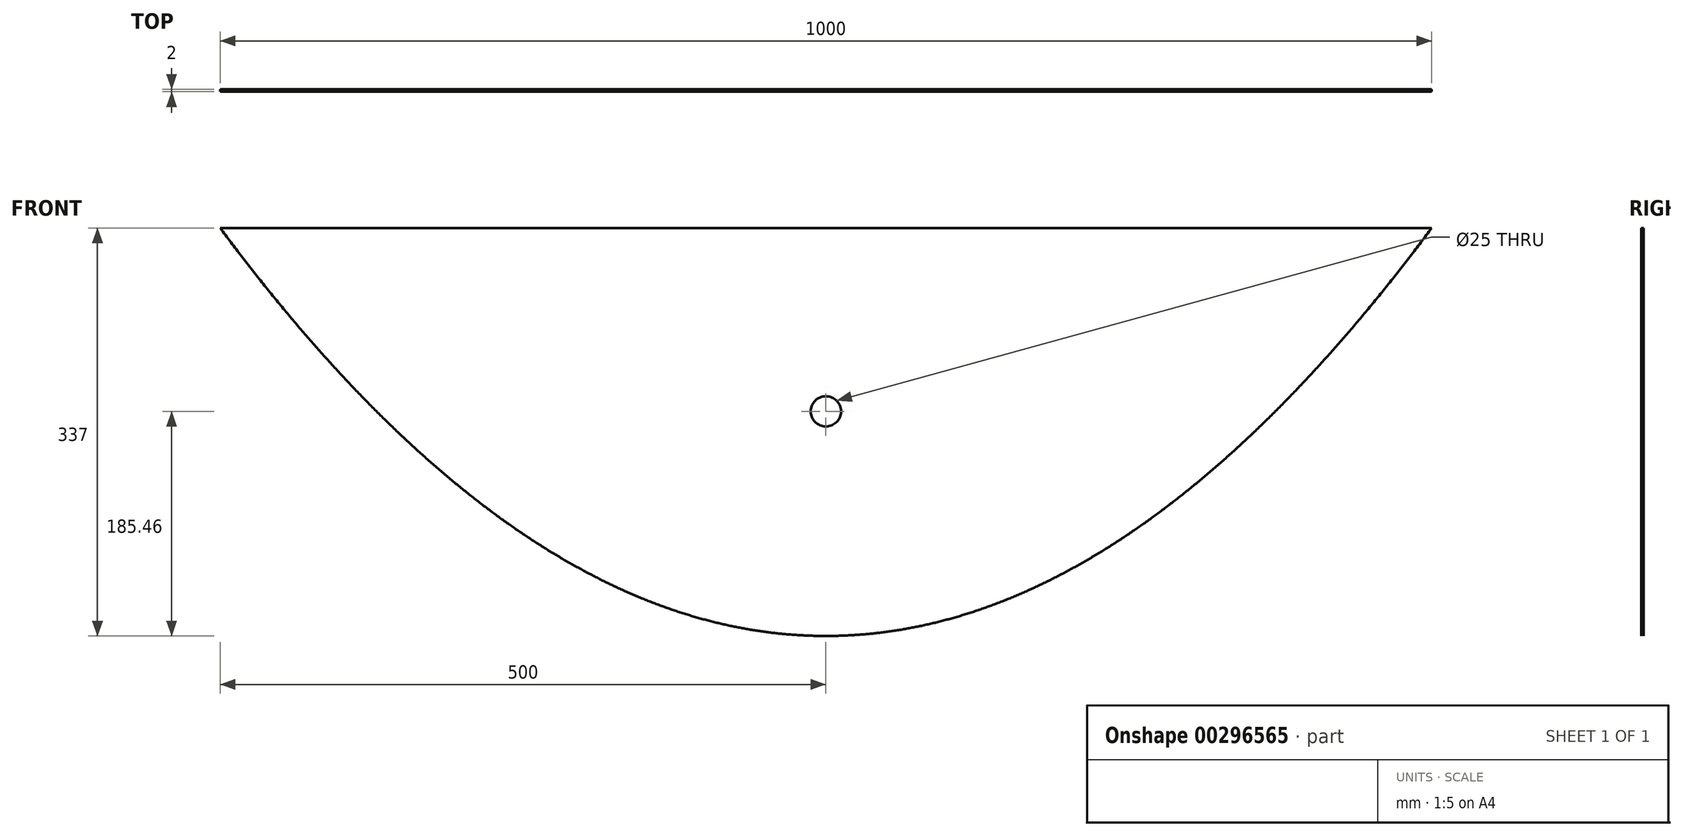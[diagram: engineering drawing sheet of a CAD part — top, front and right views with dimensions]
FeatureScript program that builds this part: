
annotation { "Feature Type Name" : "Feature", "Feature Type Description" : "" }
export const myFeature = defineFeature(function(context is Context, id is Id, definition is map)
    precondition{}
    {
        {
            var Q0;
            Q0=qCreatedBy(makeId("Front.planeOp"),FACE);
            var sketch = newSketch(context, id + "F0", { "sketchPlane" : qUnion([Q0])});
            skLineSegment(sketch, "E0", {"start": v(-500, 168.5) * mm, "end": v(-498.89, 167) * mm});
            skLineSegment(sketch, "E1", {"start": v(-498.89, 167) * mm, "end": v(-497.78, 165.5) * mm});
            skLineSegment(sketch, "E2", {"start": v(-497.78, 165.5) * mm, "end": v(-496.67, 164.02) * mm});
            skLineSegment(sketch, "E3", {"start": v(-496.67, 164.02) * mm, "end": v(-495.56, 162.53) * mm});
            skLineSegment(sketch, "E4", {"start": v(-495.56, 162.53) * mm, "end": v(-494.44, 161.05) * mm});
            skLineSegment(sketch, "E5", {"start": v(-494.44, 161.05) * mm, "end": v(-493.33, 159.57) * mm});
            skLineSegment(sketch, "E6", {"start": v(-493.33, 159.57) * mm, "end": v(-492.22, 158.1) * mm});
            skLineSegment(sketch, "E7", {"start": v(-492.22, 158.1) * mm, "end": v(-491.11, 156.62) * mm});
            skLineSegment(sketch, "E8", {"start": v(-491.11, 156.62) * mm, "end": v(-490, 155.15) * mm});
            skLineSegment(sketch, "E9", {"start": v(-490, 155.15) * mm, "end": v(-488.89, 153.69) * mm});
            skLineSegment(sketch, "E10", {"start": v(-488.89, 153.69) * mm, "end": v(-487.78, 152.22) * mm});
            skLineSegment(sketch, "E11", {"start": v(-487.78, 152.22) * mm, "end": v(-486.67, 150.76) * mm});
            skLineSegment(sketch, "E12", {"start": v(-486.67, 150.76) * mm, "end": v(-485.56, 149.3) * mm});
            skLineSegment(sketch, "E13", {"start": v(-485.56, 149.3) * mm, "end": v(-484.44, 147.86) * mm});
            skLineSegment(sketch, "E14", {"start": v(-484.44, 147.86) * mm, "end": v(-483.33, 146.4) * mm});
            skLineSegment(sketch, "E15", {"start": v(-483.33, 146.4) * mm, "end": v(-482.22, 144.96) * mm});
            skLineSegment(sketch, "E16", {"start": v(-482.22, 144.96) * mm, "end": v(-481.11, 143.52) * mm});
            skLineSegment(sketch, "E17", {"start": v(-481.11, 143.52) * mm, "end": v(-480, 142.08) * mm});
            skLineSegment(sketch, "E18", {"start": v(-480, 142.08) * mm, "end": v(-478.89, 140.64) * mm});
            skLineSegment(sketch, "E19", {"start": v(-478.89, 140.64) * mm, "end": v(-477.78, 139.2) * mm});
            skLineSegment(sketch, "E20", {"start": v(-477.78, 139.2) * mm, "end": v(-476.67, 137.78) * mm});
            skLineSegment(sketch, "E21", {"start": v(-476.67, 137.78) * mm, "end": v(-475.56, 136.35) * mm});
            skLineSegment(sketch, "E22", {"start": v(-475.56, 136.35) * mm, "end": v(-474.44, 134.93) * mm});
            skLineSegment(sketch, "E23", {"start": v(-474.44, 134.93) * mm, "end": v(-473.33, 133.5) * mm});
            skLineSegment(sketch, "E24", {"start": v(-473.33, 133.5) * mm, "end": v(-472.22, 132.1) * mm});
            skLineSegment(sketch, "E25", {"start": v(-472.22, 132.1) * mm, "end": v(-471.11, 130.68) * mm});
            skLineSegment(sketch, "E26", {"start": v(-471.11, 130.68) * mm, "end": v(-470, 129.27) * mm});
            skLineSegment(sketch, "E27", {"start": v(-470, 129.27) * mm, "end": v(-468.89, 127.86) * mm});
            skLineSegment(sketch, "E28", {"start": v(-468.89, 127.86) * mm, "end": v(-467.78, 126.46) * mm});
            skLineSegment(sketch, "E29", {"start": v(-467.78, 126.46) * mm, "end": v(-466.67, 125.06) * mm});
            skLineSegment(sketch, "E30", {"start": v(-466.67, 125.06) * mm, "end": v(-465.56, 123.67) * mm});
            skLineSegment(sketch, "E31", {"start": v(-465.56, 123.67) * mm, "end": v(-464.44, 122.27) * mm});
            skLineSegment(sketch, "E32", {"start": v(-464.44, 122.27) * mm, "end": v(-463.33, 120.88) * mm});
            skLineSegment(sketch, "E33", {"start": v(-463.33, 120.88) * mm, "end": v(-462.22, 119.5) * mm});
            skLineSegment(sketch, "E34", {"start": v(-462.22, 119.5) * mm, "end": v(-461.11, 118.11) * mm});
            skLineSegment(sketch, "E35", {"start": v(-461.11, 118.11) * mm, "end": v(-460, 116.73) * mm});
            skLineSegment(sketch, "E36", {"start": v(-460, 116.73) * mm, "end": v(-458.89, 115.36) * mm});
            skLineSegment(sketch, "E37", {"start": v(-458.89, 115.36) * mm, "end": v(-457.78, 113.99) * mm});
            skLineSegment(sketch, "E38", {"start": v(-457.78, 113.99) * mm, "end": v(-456.67, 112.62) * mm});
            skLineSegment(sketch, "E39", {"start": v(-456.67, 112.62) * mm, "end": v(-455.56, 111.25) * mm});
            skLineSegment(sketch, "E40", {"start": v(-455.56, 111.25) * mm, "end": v(-454.44, 109.89) * mm});
            skLineSegment(sketch, "E41", {"start": v(-454.44, 109.89) * mm, "end": v(-453.33, 108.53) * mm});
            skLineSegment(sketch, "E42", {"start": v(-453.33, 108.53) * mm, "end": v(-452.22, 107.17) * mm});
            skLineSegment(sketch, "E43", {"start": v(-452.22, 107.17) * mm, "end": v(-451.11, 105.82) * mm});
            skLineSegment(sketch, "E44", {"start": v(-451.11, 105.82) * mm, "end": v(-450, 104.47) * mm});
            skLineSegment(sketch, "E45", {"start": v(-450, 104.47) * mm, "end": v(-448.89, 103.12) * mm});
            skLineSegment(sketch, "E46", {"start": v(-448.89, 103.12) * mm, "end": v(-447.78, 101.78) * mm});
            skLineSegment(sketch, "E47", {"start": v(-447.78, 101.78) * mm, "end": v(-446.67, 100.44) * mm});
            skLineSegment(sketch, "E48", {"start": v(-446.67, 100.44) * mm, "end": v(-445.56, 99.1) * mm});
            skLineSegment(sketch, "E49", {"start": v(-445.56, 99.1) * mm, "end": v(-444.44, 97.77) * mm});
            skLineSegment(sketch, "E50", {"start": v(-444.44, 97.77) * mm, "end": v(-443.33, 96.44) * mm});
            skLineSegment(sketch, "E51", {"start": v(-443.33, 96.44) * mm, "end": v(-442.22, 95.11) * mm});
            skLineSegment(sketch, "E52", {"start": v(-442.22, 95.11) * mm, "end": v(-441.11, 93.8) * mm});
            skLineSegment(sketch, "E53", {"start": v(-441.11, 93.8) * mm, "end": v(-440, 92.47) * mm});
            skLineSegment(sketch, "E54", {"start": v(-440, 92.47) * mm, "end": v(-438.89, 91.15) * mm});
            skLineSegment(sketch, "E55", {"start": v(-438.89, 91.15) * mm, "end": v(-437.78, 89.84) * mm});
            skLineSegment(sketch, "E56", {"start": v(-437.78, 89.84) * mm, "end": v(-436.67, 88.53) * mm});
            skLineSegment(sketch, "E57", {"start": v(-436.67, 88.53) * mm, "end": v(-435.56, 87.23) * mm});
            skLineSegment(sketch, "E58", {"start": v(-435.56, 87.23) * mm, "end": v(-434.44, 85.92) * mm});
            skLineSegment(sketch, "E59", {"start": v(-434.44, 85.92) * mm, "end": v(-433.33, 84.62) * mm});
            skLineSegment(sketch, "E60", {"start": v(-433.33, 84.62) * mm, "end": v(-432.22, 83.33) * mm});
            skLineSegment(sketch, "E61", {"start": v(-432.22, 83.33) * mm, "end": v(-431.11, 82.03) * mm});
            skLineSegment(sketch, "E62", {"start": v(-431.11, 82.03) * mm, "end": v(-430, 80.74) * mm});
            skLineSegment(sketch, "E63", {"start": v(-430, 80.74) * mm, "end": v(-428.89, 79.46) * mm});
            skLineSegment(sketch, "E64", {"start": v(-428.89, 79.46) * mm, "end": v(-427.78, 78.17) * mm});
            skLineSegment(sketch, "E65", {"start": v(-427.78, 78.17) * mm, "end": v(-426.67, 76.9) * mm});
            skLineSegment(sketch, "E66", {"start": v(-426.67, 76.9) * mm, "end": v(-425.56, 75.62) * mm});
            skLineSegment(sketch, "E67", {"start": v(-425.56, 75.62) * mm, "end": v(-424.44, 74.34) * mm});
            skLineSegment(sketch, "E68", {"start": v(-424.44, 74.34) * mm, "end": v(-423.33, 73.07) * mm});
            skLineSegment(sketch, "E69", {"start": v(-423.33, 73.07) * mm, "end": v(-422.22, 71.8) * mm});
            skLineSegment(sketch, "E70", {"start": v(-422.22, 71.8) * mm, "end": v(-421.11, 70.54) * mm});
            skLineSegment(sketch, "E71", {"start": v(-421.11, 70.54) * mm, "end": v(-420, 69.29) * mm});
            skLineSegment(sketch, "E72", {"start": v(-420, 69.29) * mm, "end": v(-418.89, 68.03) * mm});
            skLineSegment(sketch, "E73", {"start": v(-418.89, 68.03) * mm, "end": v(-417.78, 66.78) * mm});
            skLineSegment(sketch, "E74", {"start": v(-417.78, 66.78) * mm, "end": v(-416.67, 65.53) * mm});
            skLineSegment(sketch, "E75", {"start": v(-416.67, 65.53) * mm, "end": v(-415.56, 64.28) * mm});
            skLineSegment(sketch, "E76", {"start": v(-415.56, 64.28) * mm, "end": v(-414.44, 63.04) * mm});
            skLineSegment(sketch, "E77", {"start": v(-414.44, 63.04) * mm, "end": v(-413.33, 61.8) * mm});
            skLineSegment(sketch, "E78", {"start": v(-413.33, 61.8) * mm, "end": v(-412.22, 60.56) * mm});
            skLineSegment(sketch, "E79", {"start": v(-412.22, 60.56) * mm, "end": v(-411.11, 59.33) * mm});
            skLineSegment(sketch, "E80", {"start": v(-411.11, 59.33) * mm, "end": v(-410, 58.1) * mm});
            skLineSegment(sketch, "E81", {"start": v(-410, 58.1) * mm, "end": v(-408.89, 56.87) * mm});
            skLineSegment(sketch, "E82", {"start": v(-408.89, 56.87) * mm, "end": v(-407.78, 55.65) * mm});
            skLineSegment(sketch, "E83", {"start": v(-407.78, 55.65) * mm, "end": v(-406.67, 54.43) * mm});
            skLineSegment(sketch, "E84", {"start": v(-406.67, 54.43) * mm, "end": v(-405.56, 53.21) * mm});
            skLineSegment(sketch, "E85", {"start": v(-405.56, 53.21) * mm, "end": v(-404.44, 52) * mm});
            skLineSegment(sketch, "E86", {"start": v(-404.44, 52) * mm, "end": v(-403.33, 50.79) * mm});
            skLineSegment(sketch, "E87", {"start": v(-403.33, 50.79) * mm, "end": v(-402.22, 49.58) * mm});
            skLineSegment(sketch, "E88", {"start": v(-402.22, 49.58) * mm, "end": v(-401.11, 48.38) * mm});
            skLineSegment(sketch, "E89", {"start": v(-401.11, 48.38) * mm, "end": v(-400, 47.18) * mm});
            skLineSegment(sketch, "E90", {"start": v(-400, 47.18) * mm, "end": v(-398.89, 45.98) * mm});
            skLineSegment(sketch, "E91", {"start": v(-398.89, 45.98) * mm, "end": v(-397.78, 44.79) * mm});
            skLineSegment(sketch, "E92", {"start": v(-397.78, 44.79) * mm, "end": v(-396.67, 43.6) * mm});
            skLineSegment(sketch, "E93", {"start": v(-396.67, 43.6) * mm, "end": v(-395.56, 42.41) * mm});
            skLineSegment(sketch, "E94", {"start": v(-395.56, 42.41) * mm, "end": v(-394.44, 41.23) * mm});
            skLineSegment(sketch, "E95", {"start": v(-394.44, 41.23) * mm, "end": v(-393.33, 40.05) * mm});
            skLineSegment(sketch, "E96", {"start": v(-393.33, 40.05) * mm, "end": v(-392.22, 38.87) * mm});
            skLineSegment(sketch, "E97", {"start": v(-392.22, 38.87) * mm, "end": v(-391.11, 37.7) * mm});
            skLineSegment(sketch, "E98", {"start": v(-391.11, 37.7) * mm, "end": v(-390, 36.53) * mm});
            skLineSegment(sketch, "E99", {"start": v(-390, 36.53) * mm, "end": v(-388.89, 35.36) * mm});
            skLineSegment(sketch, "E100", {"start": v(-388.89, 35.36) * mm, "end": v(-387.78, 34.2) * mm});
            skLineSegment(sketch, "E101", {"start": v(-387.78, 34.2) * mm, "end": v(-386.67, 33.04) * mm});
            skLineSegment(sketch, "E102", {"start": v(-386.67, 33.04) * mm, "end": v(-385.56, 31.88) * mm});
            skLineSegment(sketch, "E103", {"start": v(-385.56, 31.88) * mm, "end": v(-384.44, 30.73) * mm});
            skLineSegment(sketch, "E104", {"start": v(-384.44, 30.73) * mm, "end": v(-383.33, 29.58) * mm});
            skLineSegment(sketch, "E105", {"start": v(-383.33, 29.58) * mm, "end": v(-382.22, 28.43) * mm});
            skLineSegment(sketch, "E106", {"start": v(-382.22, 28.43) * mm, "end": v(-381.11, 27.29) * mm});
            skLineSegment(sketch, "E107", {"start": v(-381.11, 27.29) * mm, "end": v(-380, 26.15) * mm});
            skLineSegment(sketch, "E108", {"start": v(-380, 26.15) * mm, "end": v(-378.89, 25.01) * mm});
            skLineSegment(sketch, "E109", {"start": v(-378.89, 25.01) * mm, "end": v(-377.78, 23.88) * mm});
            skLineSegment(sketch, "E110", {"start": v(-377.78, 23.88) * mm, "end": v(-376.67, 22.75) * mm});
            skLineSegment(sketch, "E111", {"start": v(-376.67, 22.75) * mm, "end": v(-375.56, 21.62) * mm});
            skLineSegment(sketch, "E112", {"start": v(-375.56, 21.62) * mm, "end": v(-374.44, 20.5) * mm});
            skLineSegment(sketch, "E113", {"start": v(-374.44, 20.5) * mm, "end": v(-373.33, 19.38) * mm});
            skLineSegment(sketch, "E114", {"start": v(-373.33, 19.38) * mm, "end": v(-372.22, 18.26) * mm});
            skLineSegment(sketch, "E115", {"start": v(-372.22, 18.26) * mm, "end": v(-371.11, 17.15) * mm});
            skLineSegment(sketch, "E116", {"start": v(-371.11, 17.15) * mm, "end": v(-370, 16.04) * mm});
            skLineSegment(sketch, "E117", {"start": v(-370, 16.04) * mm, "end": v(-368.89, 14.93) * mm});
            skLineSegment(sketch, "E118", {"start": v(-368.89, 14.93) * mm, "end": v(-367.78, 13.83) * mm});
            skLineSegment(sketch, "E119", {"start": v(-367.78, 13.83) * mm, "end": v(-366.67, 12.73) * mm});
            skLineSegment(sketch, "E120", {"start": v(-366.67, 12.73) * mm, "end": v(-365.56, 11.63) * mm});
            skLineSegment(sketch, "E121", {"start": v(-365.56, 11.63) * mm, "end": v(-364.44, 10.54) * mm});
            skLineSegment(sketch, "E122", {"start": v(-364.44, 10.54) * mm, "end": v(-363.33, 9.45) * mm});
            skLineSegment(sketch, "E123", {"start": v(-363.33, 9.45) * mm, "end": v(-362.22, 8.36) * mm});
            skLineSegment(sketch, "E124", {"start": v(-362.22, 8.36) * mm, "end": v(-361.11, 7.28) * mm});
            skLineSegment(sketch, "E125", {"start": v(-361.11, 7.28) * mm, "end": v(-360, 6.2) * mm});
            skLineSegment(sketch, "E126", {"start": v(-360, 6.2) * mm, "end": v(-358.89, 5.12) * mm});
            skLineSegment(sketch, "E127", {"start": v(-358.89, 5.12) * mm, "end": v(-357.78, 4.05) * mm});
            skLineSegment(sketch, "E128", {"start": v(-357.78, 4.05) * mm, "end": v(-356.67, 2.98) * mm});
            skLineSegment(sketch, "E129", {"start": v(-356.67, 2.98) * mm, "end": v(-355.56, 1.91) * mm});
            skLineSegment(sketch, "E130", {"start": v(-355.56, 1.91) * mm, "end": v(-354.44, 0.85) * mm});
            skLineSegment(sketch, "E131", {"start": v(-354.44, 0.85) * mm, "end": v(-353.33, -0.21) * mm});
            skLineSegment(sketch, "E132", {"start": v(-353.33, -0.21) * mm, "end": v(-352.22, -1.27) * mm});
            skLineSegment(sketch, "E133", {"start": v(-352.22, -1.27) * mm, "end": v(-351.11, -2.32) * mm});
            skLineSegment(sketch, "E134", {"start": v(-351.11, -2.32) * mm, "end": v(-350, -3.37) * mm});
            skLineSegment(sketch, "E135", {"start": v(-350, -3.37) * mm, "end": v(-348.89, -4.42) * mm});
            skLineSegment(sketch, "E136", {"start": v(-348.89, -4.42) * mm, "end": v(-347.78, -5.46) * mm});
            skLineSegment(sketch, "E137", {"start": v(-347.78, -5.46) * mm, "end": v(-346.67, -6.5) * mm});
            skLineSegment(sketch, "E138", {"start": v(-346.67, -6.5) * mm, "end": v(-345.56, -7.54) * mm});
            skLineSegment(sketch, "E139", {"start": v(-345.56, -7.54) * mm, "end": v(-344.44, -8.57) * mm});
            skLineSegment(sketch, "E140", {"start": v(-344.44, -8.57) * mm, "end": v(-343.33, -9.6) * mm});
            skLineSegment(sketch, "E141", {"start": v(-343.33, -9.6) * mm, "end": v(-342.22, -10.63) * mm});
            skLineSegment(sketch, "E142", {"start": v(-342.22, -10.63) * mm, "end": v(-341.11, -11.65) * mm});
            skLineSegment(sketch, "E143", {"start": v(-341.11, -11.65) * mm, "end": v(-340, -12.67) * mm});
            skLineSegment(sketch, "E144", {"start": v(-340, -12.67) * mm, "end": v(-338.89, -13.7) * mm});
            skLineSegment(sketch, "E145", {"start": v(-338.89, -13.7) * mm, "end": v(-337.78, -14.7) * mm});
            skLineSegment(sketch, "E146", {"start": v(-337.78, -14.7) * mm, "end": v(-336.67, -15.71) * mm});
            skLineSegment(sketch, "E147", {"start": v(-336.67, -15.71) * mm, "end": v(-335.56, -16.72) * mm});
            skLineSegment(sketch, "E148", {"start": v(-335.56, -16.72) * mm, "end": v(-334.44, -17.72) * mm});
            skLineSegment(sketch, "E149", {"start": v(-334.44, -17.72) * mm, "end": v(-333.33, -18.72) * mm});
            skLineSegment(sketch, "E150", {"start": v(-333.33, -18.72) * mm, "end": v(-332.22, -19.72) * mm});
            skLineSegment(sketch, "E151", {"start": v(-332.22, -19.72) * mm, "end": v(-331.11, -20.71) * mm});
            skLineSegment(sketch, "E152", {"start": v(-331.11, -20.71) * mm, "end": v(-330, -21.7) * mm});
            skLineSegment(sketch, "E153", {"start": v(-330, -21.7) * mm, "end": v(-328.89, -22.7) * mm});
            skLineSegment(sketch, "E154", {"start": v(-328.89, -22.7) * mm, "end": v(-327.78, -23.68) * mm});
            skLineSegment(sketch, "E155", {"start": v(-327.78, -23.68) * mm, "end": v(-326.67, -24.66) * mm});
            skLineSegment(sketch, "E156", {"start": v(-326.67, -24.66) * mm, "end": v(-325.56, -25.63) * mm});
            skLineSegment(sketch, "E157", {"start": v(-325.56, -25.63) * mm, "end": v(-324.44, -26.6) * mm});
            skLineSegment(sketch, "E158", {"start": v(-324.44, -26.6) * mm, "end": v(-323.33, -27.58) * mm});
            skLineSegment(sketch, "E159", {"start": v(-323.33, -27.58) * mm, "end": v(-322.22, -28.54) * mm});
            skLineSegment(sketch, "E160", {"start": v(-322.22, -28.54) * mm, "end": v(-321.11, -29.5) * mm});
            skLineSegment(sketch, "E161", {"start": v(-321.11, -29.5) * mm, "end": v(-320, -30.47) * mm});
            skLineSegment(sketch, "E162", {"start": v(-320, -30.47) * mm, "end": v(-318.89, -31.42) * mm});
            skLineSegment(sketch, "E163", {"start": v(-318.89, -31.42) * mm, "end": v(-317.78, -32.38) * mm});
            skLineSegment(sketch, "E164", {"start": v(-317.78, -32.38) * mm, "end": v(-316.67, -33.33) * mm});
            skLineSegment(sketch, "E165", {"start": v(-316.67, -33.33) * mm, "end": v(-315.56, -34.27) * mm});
            skLineSegment(sketch, "E166", {"start": v(-315.56, -34.27) * mm, "end": v(-314.44, -35.22) * mm});
            skLineSegment(sketch, "E167", {"start": v(-314.44, -35.22) * mm, "end": v(-313.33, -36.16) * mm});
            skLineSegment(sketch, "E168", {"start": v(-313.33, -36.16) * mm, "end": v(-312.22, -37.1) * mm});
            skLineSegment(sketch, "E169", {"start": v(-312.22, -37.1) * mm, "end": v(-311.11, -38.03) * mm});
            skLineSegment(sketch, "E170", {"start": v(-311.11, -38.03) * mm, "end": v(-310, -38.96) * mm});
            skLineSegment(sketch, "E171", {"start": v(-310, -38.96) * mm, "end": v(-308.89, -39.89) * mm});
            skLineSegment(sketch, "E172", {"start": v(-308.89, -39.89) * mm, "end": v(-307.78, -40.8) * mm});
            skLineSegment(sketch, "E173", {"start": v(-307.78, -40.8) * mm, "end": v(-306.67, -41.73) * mm});
            skLineSegment(sketch, "E174", {"start": v(-306.67, -41.73) * mm, "end": v(-305.56, -42.65) * mm});
            skLineSegment(sketch, "E175", {"start": v(-305.56, -42.65) * mm, "end": v(-304.44, -43.56) * mm});
            skLineSegment(sketch, "E176", {"start": v(-304.44, -43.56) * mm, "end": v(-303.33, -44.47) * mm});
            skLineSegment(sketch, "E177", {"start": v(-303.33, -44.47) * mm, "end": v(-302.22, -45.38) * mm});
            skLineSegment(sketch, "E178", {"start": v(-302.22, -45.38) * mm, "end": v(-301.11, -46.28) * mm});
            skLineSegment(sketch, "E179", {"start": v(-301.11, -46.28) * mm, "end": v(-300, -47.18) * mm});
            skLineSegment(sketch, "E180", {"start": v(-300, -47.18) * mm, "end": v(-298.89, -48.08) * mm});
            skLineSegment(sketch, "E181", {"start": v(-298.89, -48.08) * mm, "end": v(-297.78, -48.97) * mm});
            skLineSegment(sketch, "E182", {"start": v(-297.78, -48.97) * mm, "end": v(-296.67, -49.86) * mm});
            skLineSegment(sketch, "E183", {"start": v(-296.67, -49.86) * mm, "end": v(-295.56, -50.75) * mm});
            skLineSegment(sketch, "E184", {"start": v(-295.56, -50.75) * mm, "end": v(-294.44, -51.63) * mm});
            skLineSegment(sketch, "E185", {"start": v(-294.44, -51.63) * mm, "end": v(-293.33, -52.51) * mm});
            skLineSegment(sketch, "E186", {"start": v(-293.33, -52.51) * mm, "end": v(-292.22, -53.4) * mm});
            skLineSegment(sketch, "E187", {"start": v(-292.22, -53.4) * mm, "end": v(-291.11, -54.26) * mm});
            skLineSegment(sketch, "E188", {"start": v(-291.11, -54.26) * mm, "end": v(-290, -55.14) * mm});
            skLineSegment(sketch, "E189", {"start": v(-290, -55.14) * mm, "end": v(-288.89, -56) * mm});
            skLineSegment(sketch, "E190", {"start": v(-288.89, -56) * mm, "end": v(-287.78, -56.87) * mm});
            skLineSegment(sketch, "E191", {"start": v(-287.78, -56.87) * mm, "end": v(-286.67, -57.73) * mm});
            skLineSegment(sketch, "E192", {"start": v(-286.67, -57.73) * mm, "end": v(-285.56, -58.58) * mm});
            skLineSegment(sketch, "E193", {"start": v(-285.56, -58.58) * mm, "end": v(-284.44, -59.44) * mm});
            skLineSegment(sketch, "E194", {"start": v(-284.44, -59.44) * mm, "end": v(-283.33, -60.29) * mm});
            skLineSegment(sketch, "E195", {"start": v(-283.33, -60.29) * mm, "end": v(-282.22, -61.13) * mm});
            skLineSegment(sketch, "E196", {"start": v(-282.22, -61.13) * mm, "end": v(-281.11, -61.98) * mm});
            skLineSegment(sketch, "E197", {"start": v(-281.11, -61.98) * mm, "end": v(-280, -62.82) * mm});
            skLineSegment(sketch, "E198", {"start": v(-280, -62.82) * mm, "end": v(-278.89, -63.66) * mm});
            skLineSegment(sketch, "E199", {"start": v(-278.89, -63.66) * mm, "end": v(-277.78, -64.49) * mm});
            skLineSegment(sketch, "E200", {"start": v(-277.78, -64.49) * mm, "end": v(-276.67, -65.32) * mm});
            skLineSegment(sketch, "E201", {"start": v(-276.67, -65.32) * mm, "end": v(-275.56, -66.15) * mm});
            skLineSegment(sketch, "E202", {"start": v(-275.56, -66.15) * mm, "end": v(-274.44, -66.97) * mm});
            skLineSegment(sketch, "E203", {"start": v(-274.44, -66.97) * mm, "end": v(-273.33, -67.8) * mm});
            skLineSegment(sketch, "E204", {"start": v(-273.33, -67.8) * mm, "end": v(-272.22, -68.6) * mm});
            skLineSegment(sketch, "E205", {"start": v(-272.22, -68.6) * mm, "end": v(-271.11, -69.42) * mm});
            skLineSegment(sketch, "E206", {"start": v(-271.11, -69.42) * mm, "end": v(-270, -70.23) * mm});
            skLineSegment(sketch, "E207", {"start": v(-270, -70.23) * mm, "end": v(-268.89, -71.04) * mm});
            skLineSegment(sketch, "E208", {"start": v(-268.89, -71.04) * mm, "end": v(-267.78, -71.84) * mm});
            skLineSegment(sketch, "E209", {"start": v(-267.78, -71.84) * mm, "end": v(-266.67, -72.64) * mm});
            skLineSegment(sketch, "E210", {"start": v(-266.67, -72.64) * mm, "end": v(-265.56, -73.44) * mm});
            skLineSegment(sketch, "E211", {"start": v(-265.56, -73.44) * mm, "end": v(-264.44, -74.24) * mm});
            skLineSegment(sketch, "E212", {"start": v(-264.44, -74.24) * mm, "end": v(-263.33, -75.03) * mm});
            skLineSegment(sketch, "E213", {"start": v(-263.33, -75.03) * mm, "end": v(-262.22, -75.81) * mm});
            skLineSegment(sketch, "E214", {"start": v(-262.22, -75.81) * mm, "end": v(-261.11, -76.6) * mm});
            skLineSegment(sketch, "E215", {"start": v(-261.11, -76.6) * mm, "end": v(-260, -77.38) * mm});
            skLineSegment(sketch, "E216", {"start": v(-260, -77.38) * mm, "end": v(-258.89, -78.15) * mm});
            skLineSegment(sketch, "E217", {"start": v(-258.89, -78.15) * mm, "end": v(-257.78, -78.93) * mm});
            skLineSegment(sketch, "E218", {"start": v(-257.78, -78.93) * mm, "end": v(-256.67, -79.7) * mm});
            skLineSegment(sketch, "E219", {"start": v(-256.67, -79.7) * mm, "end": v(-255.56, -80.47) * mm});
            skLineSegment(sketch, "E220", {"start": v(-255.56, -80.47) * mm, "end": v(-254.44, -81.23) * mm});
            skLineSegment(sketch, "E221", {"start": v(-254.44, -81.23) * mm, "end": v(-253.33, -82) * mm});
            skLineSegment(sketch, "E222", {"start": v(-253.33, -82) * mm, "end": v(-252.22, -82.75) * mm});
            skLineSegment(sketch, "E223", {"start": v(-252.22, -82.75) * mm, "end": v(-251.11, -83.5) * mm});
            skLineSegment(sketch, "E224", {"start": v(-251.11, -83.5) * mm, "end": v(-250, -84.25) * mm});
            skLineSegment(sketch, "E225", {"start": v(-250, -84.25) * mm, "end": v(-248.89, -85) * mm});
            skLineSegment(sketch, "E226", {"start": v(-248.89, -85) * mm, "end": v(-247.78, -85.74) * mm});
            skLineSegment(sketch, "E227", {"start": v(-247.78, -85.74) * mm, "end": v(-246.67, -86.48) * mm});
            skLineSegment(sketch, "E228", {"start": v(-246.67, -86.48) * mm, "end": v(-245.56, -87.22) * mm});
            skLineSegment(sketch, "E229", {"start": v(-245.56, -87.22) * mm, "end": v(-244.44, -87.95) * mm});
            skLineSegment(sketch, "E230", {"start": v(-244.44, -87.95) * mm, "end": v(-243.33, -88.69) * mm});
            skLineSegment(sketch, "E231", {"start": v(-243.33, -88.69) * mm, "end": v(-242.22, -89.41) * mm});
            skLineSegment(sketch, "E232", {"start": v(-242.22, -89.41) * mm, "end": v(-241.11, -90.14) * mm});
            skLineSegment(sketch, "E233", {"start": v(-241.11, -90.14) * mm, "end": v(-240, -90.86) * mm});
            skLineSegment(sketch, "E234", {"start": v(-240, -90.86) * mm, "end": v(-238.89, -91.57) * mm});
            skLineSegment(sketch, "E235", {"start": v(-238.89, -91.57) * mm, "end": v(-237.78, -92.29) * mm});
            skLineSegment(sketch, "E236", {"start": v(-237.78, -92.29) * mm, "end": v(-236.67, -93) * mm});
            skLineSegment(sketch, "E237", {"start": v(-236.67, -93) * mm, "end": v(-235.56, -93.7) * mm});
            skLineSegment(sketch, "E238", {"start": v(-235.56, -93.7) * mm, "end": v(-234.44, -94.41) * mm});
            skLineSegment(sketch, "E239", {"start": v(-234.44, -94.41) * mm, "end": v(-233.33, -95.11) * mm});
            skLineSegment(sketch, "E240", {"start": v(-233.33, -95.11) * mm, "end": v(-232.22, -95.8) * mm});
            skLineSegment(sketch, "E241", {"start": v(-232.22, -95.8) * mm, "end": v(-231.11, -96.5) * mm});
            skLineSegment(sketch, "E242", {"start": v(-231.11, -96.5) * mm, "end": v(-230, -97.2) * mm});
            skLineSegment(sketch, "E243", {"start": v(-230, -97.2) * mm, "end": v(-228.89, -97.88) * mm});
            skLineSegment(sketch, "E244", {"start": v(-228.89, -97.88) * mm, "end": v(-227.78, -98.56) * mm});
            skLineSegment(sketch, "E245", {"start": v(-227.78, -98.56) * mm, "end": v(-226.67, -99.24) * mm});
            skLineSegment(sketch, "E246", {"start": v(-226.67, -99.24) * mm, "end": v(-225.56, -99.92) * mm});
            skLineSegment(sketch, "E247", {"start": v(-225.56, -99.92) * mm, "end": v(-224.44, -100.6) * mm});
            skLineSegment(sketch, "E248", {"start": v(-224.44, -100.6) * mm, "end": v(-223.33, -101.27) * mm});
            skLineSegment(sketch, "E249", {"start": v(-223.33, -101.27) * mm, "end": v(-222.22, -101.93) * mm});
            skLineSegment(sketch, "E250", {"start": v(-222.22, -101.93) * mm, "end": v(-221.11, -102.6) * mm});
            skLineSegment(sketch, "E251", {"start": v(-221.11, -102.6) * mm, "end": v(-220, -103.26) * mm});
            skLineSegment(sketch, "E252", {"start": v(-220, -103.26) * mm, "end": v(-218.89, -103.92) * mm});
            skLineSegment(sketch, "E253", {"start": v(-218.89, -103.92) * mm, "end": v(-217.78, -104.57) * mm});
            skLineSegment(sketch, "E254", {"start": v(-217.78, -104.57) * mm, "end": v(-216.67, -105.22) * mm});
            skLineSegment(sketch, "E255", {"start": v(-216.67, -105.22) * mm, "end": v(-215.56, -105.87) * mm});
            skLineSegment(sketch, "E256", {"start": v(-215.56, -105.87) * mm, "end": v(-214.44, -106.51) * mm});
            skLineSegment(sketch, "E257", {"start": v(-214.44, -106.51) * mm, "end": v(-213.33, -107.15) * mm});
            skLineSegment(sketch, "E258", {"start": v(-213.33, -107.15) * mm, "end": v(-212.22, -107.8) * mm});
            skLineSegment(sketch, "E259", {"start": v(-212.22, -107.8) * mm, "end": v(-211.11, -108.42) * mm});
            skLineSegment(sketch, "E260", {"start": v(-211.11, -108.42) * mm, "end": v(-210, -109.06) * mm});
            skLineSegment(sketch, "E261", {"start": v(-210, -109.06) * mm, "end": v(-208.89, -109.68) * mm});
            skLineSegment(sketch, "E262", {"start": v(-208.89, -109.68) * mm, "end": v(-207.78, -110.3) * mm});
            skLineSegment(sketch, "E263", {"start": v(-207.78, -110.3) * mm, "end": v(-206.67, -110.93) * mm});
            skLineSegment(sketch, "E264", {"start": v(-206.67, -110.93) * mm, "end": v(-205.56, -111.54) * mm});
            skLineSegment(sketch, "E265", {"start": v(-205.56, -111.54) * mm, "end": v(-204.44, -112.16) * mm});
            skLineSegment(sketch, "E266", {"start": v(-204.44, -112.16) * mm, "end": v(-203.33, -112.77) * mm});
            skLineSegment(sketch, "E267", {"start": v(-203.33, -112.77) * mm, "end": v(-202.22, -113.38) * mm});
            skLineSegment(sketch, "E268", {"start": v(-202.22, -113.38) * mm, "end": v(-201.11, -113.98) * mm});
            skLineSegment(sketch, "E269", {"start": v(-201.11, -113.98) * mm, "end": v(-200, -114.58) * mm});
            skLineSegment(sketch, "E270", {"start": v(-200, -114.58) * mm, "end": v(-198.89, -115.18) * mm});
            skLineSegment(sketch, "E271", {"start": v(-198.89, -115.18) * mm, "end": v(-197.78, -115.77) * mm});
            skLineSegment(sketch, "E272", {"start": v(-197.78, -115.77) * mm, "end": v(-196.67, -116.36) * mm});
            skLineSegment(sketch, "E273", {"start": v(-196.67, -116.36) * mm, "end": v(-195.56, -116.95) * mm});
            skLineSegment(sketch, "E274", {"start": v(-195.56, -116.95) * mm, "end": v(-194.44, -117.54) * mm});
            skLineSegment(sketch, "E275", {"start": v(-194.44, -117.54) * mm, "end": v(-193.33, -118.12) * mm});
            skLineSegment(sketch, "E276", {"start": v(-193.33, -118.12) * mm, "end": v(-192.22, -118.7) * mm});
            skLineSegment(sketch, "E277", {"start": v(-192.22, -118.7) * mm, "end": v(-191.11, -119.27) * mm});
            skLineSegment(sketch, "E278", {"start": v(-191.11, -119.27) * mm, "end": v(-190, -119.84) * mm});
            skLineSegment(sketch, "E279", {"start": v(-190, -119.84) * mm, "end": v(-188.89, -120.4) * mm});
            skLineSegment(sketch, "E280", {"start": v(-188.89, -120.4) * mm, "end": v(-187.78, -120.97) * mm});
            skLineSegment(sketch, "E281", {"start": v(-187.78, -120.97) * mm, "end": v(-186.67, -121.53) * mm});
            skLineSegment(sketch, "E282", {"start": v(-186.67, -121.53) * mm, "end": v(-185.56, -122.09) * mm});
            skLineSegment(sketch, "E283", {"start": v(-185.56, -122.09) * mm, "end": v(-184.44, -122.64) * mm});
            skLineSegment(sketch, "E284", {"start": v(-184.44, -122.64) * mm, "end": v(-183.33, -123.2) * mm});
            skLineSegment(sketch, "E285", {"start": v(-183.33, -123.2) * mm, "end": v(-182.22, -123.74) * mm});
            skLineSegment(sketch, "E286", {"start": v(-182.22, -123.74) * mm, "end": v(-181.11, -124.29) * mm});
            skLineSegment(sketch, "E287", {"start": v(-181.11, -124.29) * mm, "end": v(-180, -124.83) * mm});
            skLineSegment(sketch, "E288", {"start": v(-180, -124.83) * mm, "end": v(-178.89, -125.36) * mm});
            skLineSegment(sketch, "E289", {"start": v(-178.89, -125.36) * mm, "end": v(-177.78, -125.9) * mm});
            skLineSegment(sketch, "E290", {"start": v(-177.78, -125.9) * mm, "end": v(-176.67, -126.43) * mm});
            skLineSegment(sketch, "E291", {"start": v(-176.67, -126.43) * mm, "end": v(-175.56, -126.96) * mm});
            skLineSegment(sketch, "E292", {"start": v(-175.56, -126.96) * mm, "end": v(-174.44, -127.48) * mm});
            skLineSegment(sketch, "E293", {"start": v(-174.44, -127.48) * mm, "end": v(-173.33, -128) * mm});
            skLineSegment(sketch, "E294", {"start": v(-173.33, -128) * mm, "end": v(-172.22, -128.52) * mm});
            skLineSegment(sketch, "E295", {"start": v(-172.22, -128.52) * mm, "end": v(-171.11, -129.03) * mm});
            skLineSegment(sketch, "E296", {"start": v(-171.11, -129.03) * mm, "end": v(-170, -129.54) * mm});
            skLineSegment(sketch, "E297", {"start": v(-170, -129.54) * mm, "end": v(-168.89, -130.05) * mm});
            skLineSegment(sketch, "E298", {"start": v(-168.89, -130.05) * mm, "end": v(-167.78, -130.56) * mm});
            skLineSegment(sketch, "E299", {"start": v(-167.78, -130.56) * mm, "end": v(-166.67, -131.06) * mm});
            skLineSegment(sketch, "E300", {"start": v(-166.67, -131.06) * mm, "end": v(-165.56, -131.56) * mm});
            skLineSegment(sketch, "E301", {"start": v(-165.56, -131.56) * mm, "end": v(-164.44, -132.05) * mm});
            skLineSegment(sketch, "E302", {"start": v(-164.44, -132.05) * mm, "end": v(-163.33, -132.54) * mm});
            skLineSegment(sketch, "E303", {"start": v(-163.33, -132.54) * mm, "end": v(-162.22, -133.03) * mm});
            skLineSegment(sketch, "E304", {"start": v(-162.22, -133.03) * mm, "end": v(-161.11, -133.51) * mm});
            skLineSegment(sketch, "E305", {"start": v(-161.11, -133.51) * mm, "end": v(-160, -134) * mm});
            skLineSegment(sketch, "E306", {"start": v(-160, -134) * mm, "end": v(-158.89, -134.47) * mm});
            skLineSegment(sketch, "E307", {"start": v(-158.89, -134.47) * mm, "end": v(-157.78, -134.94) * mm});
            skLineSegment(sketch, "E308", {"start": v(-157.78, -134.94) * mm, "end": v(-156.67, -135.42) * mm});
            skLineSegment(sketch, "E309", {"start": v(-156.67, -135.42) * mm, "end": v(-155.56, -135.88) * mm});
            skLineSegment(sketch, "E310", {"start": v(-155.56, -135.88) * mm, "end": v(-154.44, -136.35) * mm});
            skLineSegment(sketch, "E311", {"start": v(-154.44, -136.35) * mm, "end": v(-153.33, -136.8) * mm});
            skLineSegment(sketch, "E312", {"start": v(-153.33, -136.8) * mm, "end": v(-152.22, -137.27) * mm});
            skLineSegment(sketch, "E313", {"start": v(-152.22, -137.27) * mm, "end": v(-151.11, -137.72) * mm});
            skLineSegment(sketch, "E314", {"start": v(-151.11, -137.72) * mm, "end": v(-150, -138.17) * mm});
            skLineSegment(sketch, "E315", {"start": v(-150, -138.17) * mm, "end": v(-148.89, -138.62) * mm});
            skLineSegment(sketch, "E316", {"start": v(-148.89, -138.62) * mm, "end": v(-147.78, -139.06) * mm});
            skLineSegment(sketch, "E317", {"start": v(-147.78, -139.06) * mm, "end": v(-146.67, -139.5) * mm});
            skLineSegment(sketch, "E318", {"start": v(-146.67, -139.5) * mm, "end": v(-145.56, -139.94) * mm});
            skLineSegment(sketch, "E319", {"start": v(-145.56, -139.94) * mm, "end": v(-144.44, -140.38) * mm});
            skLineSegment(sketch, "E320", {"start": v(-144.44, -140.38) * mm, "end": v(-143.33, -140.8) * mm});
            skLineSegment(sketch, "E321", {"start": v(-143.33, -140.8) * mm, "end": v(-142.22, -141.24) * mm});
            skLineSegment(sketch, "E322", {"start": v(-142.22, -141.24) * mm, "end": v(-141.11, -141.66) * mm});
            skLineSegment(sketch, "E323", {"start": v(-141.11, -141.66) * mm, "end": v(-140, -142.08) * mm});
            skLineSegment(sketch, "E324", {"start": v(-140, -142.08) * mm, "end": v(-138.89, -142.5) * mm});
            skLineSegment(sketch, "E325", {"start": v(-138.89, -142.5) * mm, "end": v(-137.78, -142.91) * mm});
            skLineSegment(sketch, "E326", {"start": v(-137.78, -142.91) * mm, "end": v(-136.67, -143.32) * mm});
            skLineSegment(sketch, "E327", {"start": v(-136.67, -143.32) * mm, "end": v(-135.56, -143.73) * mm});
            skLineSegment(sketch, "E328", {"start": v(-135.56, -143.73) * mm, "end": v(-134.44, -144.14) * mm});
            skLineSegment(sketch, "E329", {"start": v(-134.44, -144.14) * mm, "end": v(-133.33, -144.54) * mm});
            skLineSegment(sketch, "E330", {"start": v(-133.33, -144.54) * mm, "end": v(-132.22, -144.94) * mm});
            skLineSegment(sketch, "E331", {"start": v(-132.22, -144.94) * mm, "end": v(-131.11, -145.33) * mm});
            skLineSegment(sketch, "E332", {"start": v(-131.11, -145.33) * mm, "end": v(-130, -145.72) * mm});
            skLineSegment(sketch, "E333", {"start": v(-130, -145.72) * mm, "end": v(-128.89, -146.1) * mm});
            skLineSegment(sketch, "E334", {"start": v(-128.89, -146.1) * mm, "end": v(-127.78, -146.5) * mm});
            skLineSegment(sketch, "E335", {"start": v(-127.78, -146.5) * mm, "end": v(-126.67, -146.87) * mm});
            skLineSegment(sketch, "E336", {"start": v(-126.67, -146.87) * mm, "end": v(-125.56, -147.25) * mm});
            skLineSegment(sketch, "E337", {"start": v(-125.56, -147.25) * mm, "end": v(-124.44, -147.63) * mm});
            skLineSegment(sketch, "E338", {"start": v(-124.44, -147.63) * mm, "end": v(-123.33, -148) * mm});
            skLineSegment(sketch, "E339", {"start": v(-123.33, -148) * mm, "end": v(-122.22, -148.36) * mm});
            skLineSegment(sketch, "E340", {"start": v(-122.22, -148.36) * mm, "end": v(-121.11, -148.73) * mm});
            skLineSegment(sketch, "E341", {"start": v(-121.11, -148.73) * mm, "end": v(-120, -149.1) * mm});
            skLineSegment(sketch, "E342", {"start": v(-120, -149.1) * mm, "end": v(-118.89, -149.45) * mm});
            skLineSegment(sketch, "E343", {"start": v(-118.89, -149.45) * mm, "end": v(-117.78, -149.8) * mm});
            skLineSegment(sketch, "E344", {"start": v(-117.78, -149.8) * mm, "end": v(-116.67, -150.15) * mm});
            skLineSegment(sketch, "E345", {"start": v(-116.67, -150.15) * mm, "end": v(-115.56, -150.5) * mm});
            skLineSegment(sketch, "E346", {"start": v(-115.56, -150.5) * mm, "end": v(-114.44, -150.85) * mm});
            skLineSegment(sketch, "E347", {"start": v(-114.44, -150.85) * mm, "end": v(-113.33, -151.19) * mm});
            skLineSegment(sketch, "E348", {"start": v(-113.33, -151.19) * mm, "end": v(-112.22, -151.53) * mm});
            skLineSegment(sketch, "E349", {"start": v(-112.22, -151.53) * mm, "end": v(-111.11, -151.86) * mm});
            skLineSegment(sketch, "E350", {"start": v(-111.11, -151.86) * mm, "end": v(-110, -152.2) * mm});
            skLineSegment(sketch, "E351", {"start": v(-110, -152.2) * mm, "end": v(-108.89, -152.52) * mm});
            skLineSegment(sketch, "E352", {"start": v(-108.89, -152.52) * mm, "end": v(-107.78, -152.84) * mm});
            skLineSegment(sketch, "E353", {"start": v(-107.78, -152.84) * mm, "end": v(-106.67, -153.16) * mm});
            skLineSegment(sketch, "E354", {"start": v(-106.67, -153.16) * mm, "end": v(-105.56, -153.48) * mm});
            skLineSegment(sketch, "E355", {"start": v(-105.56, -153.48) * mm, "end": v(-104.44, -153.8) * mm});
            skLineSegment(sketch, "E356", {"start": v(-104.44, -153.8) * mm, "end": v(-103.33, -154.1) * mm});
            skLineSegment(sketch, "E357", {"start": v(-103.33, -154.1) * mm, "end": v(-102.22, -154.42) * mm});
            skLineSegment(sketch, "E358", {"start": v(-102.22, -154.42) * mm, "end": v(-101.11, -154.72) * mm});
            skLineSegment(sketch, "E359", {"start": v(-101.11, -154.72) * mm, "end": v(-100, -155.02) * mm});
            skLineSegment(sketch, "E360", {"start": v(-100, -155.02) * mm, "end": v(-98.89, -155.32) * mm});
            skLineSegment(sketch, "E361", {"start": v(-98.89, -155.32) * mm, "end": v(-97.78, -155.61) * mm});
            skLineSegment(sketch, "E362", {"start": v(-97.78, -155.61) * mm, "end": v(-96.67, -155.9) * mm});
            skLineSegment(sketch, "E363", {"start": v(-96.67, -155.9) * mm, "end": v(-95.56, -156.2) * mm});
            skLineSegment(sketch, "E364", {"start": v(-95.56, -156.2) * mm, "end": v(-94.44, -156.48) * mm});
            skLineSegment(sketch, "E365", {"start": v(-94.44, -156.48) * mm, "end": v(-93.33, -156.76) * mm});
            skLineSegment(sketch, "E366", {"start": v(-93.33, -156.76) * mm, "end": v(-92.22, -157.04) * mm});
            skLineSegment(sketch, "E367", {"start": v(-92.22, -157.04) * mm, "end": v(-91.11, -157.31) * mm});
            skLineSegment(sketch, "E368", {"start": v(-91.11, -157.31) * mm, "end": v(-90, -157.58) * mm});
            skLineSegment(sketch, "E369", {"start": v(-90, -157.58) * mm, "end": v(-88.89, -157.85) * mm});
            skLineSegment(sketch, "E370", {"start": v(-88.89, -157.85) * mm, "end": v(-87.78, -158.12) * mm});
            skLineSegment(sketch, "E371", {"start": v(-87.78, -158.12) * mm, "end": v(-86.67, -158.38) * mm});
            skLineSegment(sketch, "E372", {"start": v(-86.67, -158.38) * mm, "end": v(-85.56, -158.63) * mm});
            skLineSegment(sketch, "E373", {"start": v(-85.56, -158.63) * mm, "end": v(-84.44, -158.89) * mm});
            skLineSegment(sketch, "E374", {"start": v(-84.44, -158.89) * mm, "end": v(-83.33, -159.14) * mm});
            skLineSegment(sketch, "E375", {"start": v(-83.33, -159.14) * mm, "end": v(-82.22, -159.39) * mm});
            skLineSegment(sketch, "E376", {"start": v(-82.22, -159.39) * mm, "end": v(-81.11, -159.63) * mm});
            skLineSegment(sketch, "E377", {"start": v(-81.11, -159.63) * mm, "end": v(-80, -159.87) * mm});
            skLineSegment(sketch, "E378", {"start": v(-80, -159.87) * mm, "end": v(-78.89, -160.11) * mm});
            skLineSegment(sketch, "E379", {"start": v(-78.89, -160.11) * mm, "end": v(-77.78, -160.35) * mm});
            skLineSegment(sketch, "E380", {"start": v(-77.78, -160.35) * mm, "end": v(-76.67, -160.58) * mm});
            skLineSegment(sketch, "E381", {"start": v(-76.67, -160.58) * mm, "end": v(-75.56, -160.8) * mm});
            skLineSegment(sketch, "E382", {"start": v(-75.56, -160.8) * mm, "end": v(-74.44, -161.03) * mm});
            skLineSegment(sketch, "E383", {"start": v(-74.44, -161.03) * mm, "end": v(-73.33, -161.25) * mm});
            skLineSegment(sketch, "E384", {"start": v(-73.33, -161.25) * mm, "end": v(-72.22, -161.47) * mm});
            skLineSegment(sketch, "E385", {"start": v(-72.22, -161.47) * mm, "end": v(-71.11, -161.69) * mm});
            skLineSegment(sketch, "E386", {"start": v(-71.11, -161.69) * mm, "end": v(-70, -161.9) * mm});
            skLineSegment(sketch, "E387", {"start": v(-70, -161.9) * mm, "end": v(-68.89, -162.1) * mm});
            skLineSegment(sketch, "E388", {"start": v(-68.89, -162.1) * mm, "end": v(-67.78, -162.3) * mm});
            skLineSegment(sketch, "E389", {"start": v(-67.78, -162.3) * mm, "end": v(-66.67, -162.51) * mm});
            skLineSegment(sketch, "E390", {"start": v(-66.67, -162.51) * mm, "end": v(-65.56, -162.7) * mm});
            skLineSegment(sketch, "E391", {"start": v(-65.56, -162.7) * mm, "end": v(-64.44, -162.9) * mm});
            skLineSegment(sketch, "E392", {"start": v(-64.44, -162.9) * mm, "end": v(-63.33, -163.1) * mm});
            skLineSegment(sketch, "E393", {"start": v(-63.33, -163.1) * mm, "end": v(-62.22, -163.28) * mm});
            skLineSegment(sketch, "E394", {"start": v(-62.22, -163.28) * mm, "end": v(-61.11, -163.47) * mm});
            skLineSegment(sketch, "E395", {"start": v(-61.11, -163.47) * mm, "end": v(-60, -163.65) * mm});
            skLineSegment(sketch, "E396", {"start": v(-60, -163.65) * mm, "end": v(-58.89, -163.83) * mm});
            skLineSegment(sketch, "E397", {"start": v(-58.89, -163.83) * mm, "end": v(-57.78, -164) * mm});
            skLineSegment(sketch, "E398", {"start": v(-57.78, -164) * mm, "end": v(-56.67, -164.17) * mm});
            skLineSegment(sketch, "E399", {"start": v(-56.67, -164.17) * mm, "end": v(-55.56, -164.34) * mm});
            skLineSegment(sketch, "E400", {"start": v(-55.56, -164.34) * mm, "end": v(-54.44, -164.5) * mm});
            skLineSegment(sketch, "E401", {"start": v(-54.44, -164.5) * mm, "end": v(-53.33, -164.67) * mm});
            skLineSegment(sketch, "E402", {"start": v(-53.33, -164.67) * mm, "end": v(-52.22, -164.83) * mm});
            skLineSegment(sketch, "E403", {"start": v(-52.22, -164.83) * mm, "end": v(-51.11, -164.98) * mm});
            skLineSegment(sketch, "E404", {"start": v(-51.11, -164.98) * mm, "end": v(-50, -165.13) * mm});
            skLineSegment(sketch, "E405", {"start": v(-50, -165.13) * mm, "end": v(-48.89, -165.28) * mm});
            skLineSegment(sketch, "E406", {"start": v(-48.89, -165.28) * mm, "end": v(-47.78, -165.42) * mm});
            skLineSegment(sketch, "E407", {"start": v(-47.78, -165.42) * mm, "end": v(-46.67, -165.57) * mm});
            skLineSegment(sketch, "E408", {"start": v(-46.67, -165.57) * mm, "end": v(-45.56, -165.7) * mm});
            skLineSegment(sketch, "E409", {"start": v(-45.56, -165.7) * mm, "end": v(-44.44, -165.84) * mm});
            skLineSegment(sketch, "E410", {"start": v(-44.44, -165.84) * mm, "end": v(-43.33, -165.97) * mm});
            skLineSegment(sketch, "E411", {"start": v(-43.33, -165.97) * mm, "end": v(-42.22, -166.1) * mm});
            skLineSegment(sketch, "E412", {"start": v(-42.22, -166.1) * mm, "end": v(-41.11, -166.22) * mm});
            skLineSegment(sketch, "E413", {"start": v(-41.11, -166.22) * mm, "end": v(-40, -166.34) * mm});
            skLineSegment(sketch, "E414", {"start": v(-40, -166.34) * mm, "end": v(-38.89, -166.46) * mm});
            skLineSegment(sketch, "E415", {"start": v(-38.89, -166.46) * mm, "end": v(-37.78, -166.58) * mm});
            skLineSegment(sketch, "E416", {"start": v(-37.78, -166.58) * mm, "end": v(-36.67, -166.69) * mm});
            skLineSegment(sketch, "E417", {"start": v(-36.67, -166.69) * mm, "end": v(-35.56, -166.8) * mm});
            skLineSegment(sketch, "E418", {"start": v(-35.56, -166.8) * mm, "end": v(-34.44, -166.9) * mm});
            skLineSegment(sketch, "E419", {"start": v(-34.44, -166.9) * mm, "end": v(-33.33, -167) * mm});
            skLineSegment(sketch, "E420", {"start": v(-33.33, -167) * mm, "end": v(-32.22, -167.1) * mm});
            skLineSegment(sketch, "E421", {"start": v(-32.22, -167.1) * mm, "end": v(-31.11, -167.2) * mm});
            skLineSegment(sketch, "E422", {"start": v(-31.11, -167.2) * mm, "end": v(-30, -167.29) * mm});
            skLineSegment(sketch, "E423", {"start": v(-30, -167.29) * mm, "end": v(-28.89, -167.38) * mm});
            skLineSegment(sketch, "E424", {"start": v(-28.89, -167.38) * mm, "end": v(-27.78, -167.46) * mm});
            skLineSegment(sketch, "E425", {"start": v(-27.78, -167.46) * mm, "end": v(-26.67, -167.54) * mm});
            skLineSegment(sketch, "E426", {"start": v(-26.67, -167.54) * mm, "end": v(-25.56, -167.62) * mm});
            skLineSegment(sketch, "E427", {"start": v(-25.56, -167.62) * mm, "end": v(-24.44, -167.7) * mm});
            skLineSegment(sketch, "E428", {"start": v(-24.44, -167.7) * mm, "end": v(-23.33, -167.77) * mm});
            skLineSegment(sketch, "E429", {"start": v(-23.33, -167.77) * mm, "end": v(-22.22, -167.84) * mm});
            skLineSegment(sketch, "E430", {"start": v(-22.22, -167.84) * mm, "end": v(-21.11, -167.9) * mm});
            skLineSegment(sketch, "E431", {"start": v(-21.11, -167.9) * mm, "end": v(-20, -167.96) * mm});
            skLineSegment(sketch, "E432", {"start": v(-20, -167.96) * mm, "end": v(-18.89, -168.02) * mm});
            skLineSegment(sketch, "E433", {"start": v(-18.89, -168.02) * mm, "end": v(-17.78, -168.08) * mm});
            skLineSegment(sketch, "E434", {"start": v(-17.78, -168.08) * mm, "end": v(-16.67, -168.13) * mm});
            skLineSegment(sketch, "E435", {"start": v(-16.67, -168.13) * mm, "end": v(-15.56, -168.18) * mm});
            skLineSegment(sketch, "E436", {"start": v(-15.56, -168.18) * mm, "end": v(-14.44, -168.22) * mm});
            skLineSegment(sketch, "E437", {"start": v(-14.44, -168.22) * mm, "end": v(-13.33, -168.26) * mm});
            skLineSegment(sketch, "E438", {"start": v(-13.33, -168.26) * mm, "end": v(-12.22, -168.3) * mm});
            skLineSegment(sketch, "E439", {"start": v(-12.22, -168.3) * mm, "end": v(-11.11, -168.33) * mm});
            skLineSegment(sketch, "E440", {"start": v(-11.11, -168.33) * mm, "end": v(-10, -168.37) * mm});
            skLineSegment(sketch, "E441", {"start": v(-10, -168.37) * mm, "end": v(-8.89, -168.4) * mm});
            skLineSegment(sketch, "E442", {"start": v(-8.89, -168.4) * mm, "end": v(-7.78, -168.42) * mm});
            skLineSegment(sketch, "E443", {"start": v(-7.78, -168.42) * mm, "end": v(-6.67, -168.44) * mm});
            skLineSegment(sketch, "E444", {"start": v(-6.67, -168.44) * mm, "end": v(-5.56, -168.46) * mm});
            skLineSegment(sketch, "E445", {"start": v(-5.56, -168.46) * mm, "end": v(-4.44, -168.47) * mm});
            skLineSegment(sketch, "E446", {"start": v(-4.44, -168.47) * mm, "end": v(-3.33, -168.49) * mm});
            skLineSegment(sketch, "E447", {"start": v(-3.33, -168.49) * mm, "end": v(-2.22, -168.5) * mm});
            skLineSegment(sketch, "E448", {"start": v(-2.22, -168.5) * mm, "end": v(-1.11, -168.5) * mm});
            skLineSegment(sketch, "E449", {"start": v(-1.11, -168.5) * mm, "end": v(0, -168.5) * mm});
            skLineSegment(sketch, "E450", {"start": v(0, -168.5) * mm, "end": v(1.11, -168.5) * mm});
            skLineSegment(sketch, "E451", {"start": v(1.11, -168.5) * mm, "end": v(2.22, -168.5) * mm});
            skLineSegment(sketch, "E452", {"start": v(2.22, -168.5) * mm, "end": v(3.33, -168.49) * mm});
            skLineSegment(sketch, "E453", {"start": v(3.33, -168.49) * mm, "end": v(4.44, -168.47) * mm});
            skLineSegment(sketch, "E454", {"start": v(4.44, -168.47) * mm, "end": v(5.56, -168.46) * mm});
            skLineSegment(sketch, "E455", {"start": v(5.56, -168.46) * mm, "end": v(6.67, -168.44) * mm});
            skLineSegment(sketch, "E456", {"start": v(6.67, -168.44) * mm, "end": v(7.78, -168.42) * mm});
            skLineSegment(sketch, "E457", {"start": v(7.78, -168.42) * mm, "end": v(8.89, -168.4) * mm});
            skLineSegment(sketch, "E458", {"start": v(8.89, -168.4) * mm, "end": v(10, -168.37) * mm});
            skLineSegment(sketch, "E459", {"start": v(10, -168.37) * mm, "end": v(11.11, -168.33) * mm});
            skLineSegment(sketch, "E460", {"start": v(11.11, -168.33) * mm, "end": v(12.22, -168.3) * mm});
            skLineSegment(sketch, "E461", {"start": v(12.22, -168.3) * mm, "end": v(13.33, -168.26) * mm});
            skLineSegment(sketch, "E462", {"start": v(13.33, -168.26) * mm, "end": v(14.44, -168.22) * mm});
            skLineSegment(sketch, "E463", {"start": v(14.44, -168.22) * mm, "end": v(15.56, -168.18) * mm});
            skLineSegment(sketch, "E464", {"start": v(15.56, -168.18) * mm, "end": v(16.67, -168.13) * mm});
            skLineSegment(sketch, "E465", {"start": v(16.67, -168.13) * mm, "end": v(17.78, -168.08) * mm});
            skLineSegment(sketch, "E466", {"start": v(17.78, -168.08) * mm, "end": v(18.89, -168.02) * mm});
            skLineSegment(sketch, "E467", {"start": v(18.89, -168.02) * mm, "end": v(20, -167.96) * mm});
            skLineSegment(sketch, "E468", {"start": v(20, -167.96) * mm, "end": v(21.11, -167.9) * mm});
            skLineSegment(sketch, "E469", {"start": v(21.11, -167.9) * mm, "end": v(22.22, -167.84) * mm});
            skLineSegment(sketch, "E470", {"start": v(22.22, -167.84) * mm, "end": v(23.33, -167.77) * mm});
            skLineSegment(sketch, "E471", {"start": v(23.33, -167.77) * mm, "end": v(24.44, -167.7) * mm});
            skLineSegment(sketch, "E472", {"start": v(24.44, -167.7) * mm, "end": v(25.56, -167.62) * mm});
            skLineSegment(sketch, "E473", {"start": v(25.56, -167.62) * mm, "end": v(26.67, -167.54) * mm});
            skLineSegment(sketch, "E474", {"start": v(26.67, -167.54) * mm, "end": v(27.78, -167.46) * mm});
            skLineSegment(sketch, "E475", {"start": v(27.78, -167.46) * mm, "end": v(28.89, -167.38) * mm});
            skLineSegment(sketch, "E476", {"start": v(28.89, -167.38) * mm, "end": v(30, -167.29) * mm});
            skLineSegment(sketch, "E477", {"start": v(30, -167.29) * mm, "end": v(31.11, -167.2) * mm});
            skLineSegment(sketch, "E478", {"start": v(31.11, -167.2) * mm, "end": v(32.22, -167.1) * mm});
            skLineSegment(sketch, "E479", {"start": v(32.22, -167.1) * mm, "end": v(33.33, -167) * mm});
            skLineSegment(sketch, "E480", {"start": v(33.33, -167) * mm, "end": v(34.44, -166.9) * mm});
            skLineSegment(sketch, "E481", {"start": v(34.44, -166.9) * mm, "end": v(35.56, -166.8) * mm});
            skLineSegment(sketch, "E482", {"start": v(35.56, -166.8) * mm, "end": v(36.67, -166.69) * mm});
            skLineSegment(sketch, "E483", {"start": v(36.67, -166.69) * mm, "end": v(37.78, -166.58) * mm});
            skLineSegment(sketch, "E484", {"start": v(37.78, -166.58) * mm, "end": v(38.89, -166.46) * mm});
            skLineSegment(sketch, "E485", {"start": v(38.89, -166.46) * mm, "end": v(40, -166.34) * mm});
            skLineSegment(sketch, "E486", {"start": v(40, -166.34) * mm, "end": v(41.11, -166.22) * mm});
            skLineSegment(sketch, "E487", {"start": v(41.11, -166.22) * mm, "end": v(42.22, -166.1) * mm});
            skLineSegment(sketch, "E488", {"start": v(42.22, -166.1) * mm, "end": v(43.33, -165.97) * mm});
            skLineSegment(sketch, "E489", {"start": v(43.33, -165.97) * mm, "end": v(44.44, -165.84) * mm});
            skLineSegment(sketch, "E490", {"start": v(44.44, -165.84) * mm, "end": v(45.56, -165.7) * mm});
            skLineSegment(sketch, "E491", {"start": v(45.56, -165.7) * mm, "end": v(46.67, -165.57) * mm});
            skLineSegment(sketch, "E492", {"start": v(46.67, -165.57) * mm, "end": v(47.78, -165.42) * mm});
            skLineSegment(sketch, "E493", {"start": v(47.78, -165.42) * mm, "end": v(48.89, -165.28) * mm});
            skLineSegment(sketch, "E494", {"start": v(48.89, -165.28) * mm, "end": v(50, -165.13) * mm});
            skLineSegment(sketch, "E495", {"start": v(50, -165.13) * mm, "end": v(51.11, -164.98) * mm});
            skLineSegment(sketch, "E496", {"start": v(51.11, -164.98) * mm, "end": v(52.22, -164.82) * mm});
            skLineSegment(sketch, "E497", {"start": v(52.22, -164.82) * mm, "end": v(53.33, -164.67) * mm});
            skLineSegment(sketch, "E498", {"start": v(53.33, -164.67) * mm, "end": v(54.44, -164.5) * mm});
            skLineSegment(sketch, "E499", {"start": v(54.44, -164.5) * mm, "end": v(55.56, -164.34) * mm});
            skLineSegment(sketch, "E500", {"start": v(55.56, -164.34) * mm, "end": v(56.67, -164.17) * mm});
            skLineSegment(sketch, "E501", {"start": v(56.67, -164.17) * mm, "end": v(57.78, -164) * mm});
            skLineSegment(sketch, "E502", {"start": v(57.78, -164) * mm, "end": v(58.89, -163.83) * mm});
            skLineSegment(sketch, "E503", {"start": v(58.89, -163.83) * mm, "end": v(60, -163.65) * mm});
            skLineSegment(sketch, "E504", {"start": v(60, -163.65) * mm, "end": v(61.11, -163.47) * mm});
            skLineSegment(sketch, "E505", {"start": v(61.11, -163.47) * mm, "end": v(62.22, -163.28) * mm});
            skLineSegment(sketch, "E506", {"start": v(62.22, -163.28) * mm, "end": v(63.33, -163.1) * mm});
            skLineSegment(sketch, "E507", {"start": v(63.33, -163.1) * mm, "end": v(64.44, -162.9) * mm});
            skLineSegment(sketch, "E508", {"start": v(64.44, -162.9) * mm, "end": v(65.56, -162.7) * mm});
            skLineSegment(sketch, "E509", {"start": v(65.56, -162.7) * mm, "end": v(66.67, -162.5) * mm});
            skLineSegment(sketch, "E510", {"start": v(66.67, -162.5) * mm, "end": v(67.78, -162.3) * mm});
            skLineSegment(sketch, "E511", {"start": v(67.78, -162.3) * mm, "end": v(68.89, -162.1) * mm});
            skLineSegment(sketch, "E512", {"start": v(68.89, -162.1) * mm, "end": v(70, -161.9) * mm});
            skLineSegment(sketch, "E513", {"start": v(70, -161.9) * mm, "end": v(71.11, -161.68) * mm});
            skLineSegment(sketch, "E514", {"start": v(71.11, -161.68) * mm, "end": v(72.22, -161.47) * mm});
            skLineSegment(sketch, "E515", {"start": v(72.22, -161.47) * mm, "end": v(73.33, -161.25) * mm});
            skLineSegment(sketch, "E516", {"start": v(73.33, -161.25) * mm, "end": v(74.44, -161.03) * mm});
            skLineSegment(sketch, "E517", {"start": v(74.44, -161.03) * mm, "end": v(75.56, -160.8) * mm});
            skLineSegment(sketch, "E518", {"start": v(75.56, -160.8) * mm, "end": v(76.67, -160.58) * mm});
            skLineSegment(sketch, "E519", {"start": v(76.67, -160.58) * mm, "end": v(77.78, -160.35) * mm});
            skLineSegment(sketch, "E520", {"start": v(77.78, -160.35) * mm, "end": v(78.89, -160.11) * mm});
            skLineSegment(sketch, "E521", {"start": v(78.89, -160.11) * mm, "end": v(80, -159.87) * mm});
            skLineSegment(sketch, "E522", {"start": v(80, -159.87) * mm, "end": v(81.11, -159.63) * mm});
            skLineSegment(sketch, "E523", {"start": v(81.11, -159.63) * mm, "end": v(82.22, -159.39) * mm});
            skLineSegment(sketch, "E524", {"start": v(82.22, -159.39) * mm, "end": v(83.33, -159.14) * mm});
            skLineSegment(sketch, "E525", {"start": v(83.33, -159.14) * mm, "end": v(84.44, -158.89) * mm});
            skLineSegment(sketch, "E526", {"start": v(84.44, -158.89) * mm, "end": v(85.56, -158.63) * mm});
            skLineSegment(sketch, "E527", {"start": v(85.56, -158.63) * mm, "end": v(86.67, -158.38) * mm});
            skLineSegment(sketch, "E528", {"start": v(86.67, -158.38) * mm, "end": v(87.78, -158.11) * mm});
            skLineSegment(sketch, "E529", {"start": v(87.78, -158.11) * mm, "end": v(88.89, -157.85) * mm});
            skLineSegment(sketch, "E530", {"start": v(88.89, -157.85) * mm, "end": v(90, -157.58) * mm});
            skLineSegment(sketch, "E531", {"start": v(90, -157.58) * mm, "end": v(91.11, -157.31) * mm});
            skLineSegment(sketch, "E532", {"start": v(91.11, -157.31) * mm, "end": v(92.22, -157.04) * mm});
            skLineSegment(sketch, "E533", {"start": v(92.22, -157.04) * mm, "end": v(93.33, -156.76) * mm});
            skLineSegment(sketch, "E534", {"start": v(93.33, -156.76) * mm, "end": v(94.44, -156.48) * mm});
            skLineSegment(sketch, "E535", {"start": v(94.44, -156.48) * mm, "end": v(95.56, -156.2) * mm});
            skLineSegment(sketch, "E536", {"start": v(95.56, -156.2) * mm, "end": v(96.67, -155.9) * mm});
            skLineSegment(sketch, "E537", {"start": v(96.67, -155.9) * mm, "end": v(97.78, -155.61) * mm});
            skLineSegment(sketch, "E538", {"start": v(97.78, -155.61) * mm, "end": v(98.89, -155.32) * mm});
            skLineSegment(sketch, "E539", {"start": v(98.89, -155.32) * mm, "end": v(100, -155.02) * mm});
            skLineSegment(sketch, "E540", {"start": v(100, -155.02) * mm, "end": v(101.11, -154.72) * mm});
            skLineSegment(sketch, "E541", {"start": v(101.11, -154.72) * mm, "end": v(102.22, -154.42) * mm});
            skLineSegment(sketch, "E542", {"start": v(102.22, -154.42) * mm, "end": v(103.33, -154.1) * mm});
            skLineSegment(sketch, "E543", {"start": v(103.33, -154.1) * mm, "end": v(104.44, -153.8) * mm});
            skLineSegment(sketch, "E544", {"start": v(104.44, -153.8) * mm, "end": v(105.56, -153.48) * mm});
            skLineSegment(sketch, "E545", {"start": v(105.56, -153.48) * mm, "end": v(106.67, -153.16) * mm});
            skLineSegment(sketch, "E546", {"start": v(106.67, -153.16) * mm, "end": v(107.78, -152.84) * mm});
            skLineSegment(sketch, "E547", {"start": v(107.78, -152.84) * mm, "end": v(108.89, -152.52) * mm});
            skLineSegment(sketch, "E548", {"start": v(108.89, -152.52) * mm, "end": v(110, -152.2) * mm});
            skLineSegment(sketch, "E549", {"start": v(110, -152.2) * mm, "end": v(111.11, -151.86) * mm});
            skLineSegment(sketch, "E550", {"start": v(111.11, -151.86) * mm, "end": v(112.22, -151.52) * mm});
            skLineSegment(sketch, "E551", {"start": v(112.22, -151.52) * mm, "end": v(113.33, -151.19) * mm});
            skLineSegment(sketch, "E552", {"start": v(113.33, -151.19) * mm, "end": v(114.44, -150.85) * mm});
            skLineSegment(sketch, "E553", {"start": v(114.44, -150.85) * mm, "end": v(115.56, -150.5) * mm});
            skLineSegment(sketch, "E554", {"start": v(115.56, -150.5) * mm, "end": v(116.67, -150.15) * mm});
            skLineSegment(sketch, "E555", {"start": v(116.67, -150.15) * mm, "end": v(117.78, -149.8) * mm});
            skLineSegment(sketch, "E556", {"start": v(117.78, -149.8) * mm, "end": v(118.89, -149.45) * mm});
            skLineSegment(sketch, "E557", {"start": v(118.89, -149.45) * mm, "end": v(120, -149.09) * mm});
            skLineSegment(sketch, "E558", {"start": v(120, -149.09) * mm, "end": v(121.11, -148.73) * mm});
            skLineSegment(sketch, "E559", {"start": v(121.11, -148.73) * mm, "end": v(122.22, -148.36) * mm});
            skLineSegment(sketch, "E560", {"start": v(122.22, -148.36) * mm, "end": v(123.33, -148) * mm});
            skLineSegment(sketch, "E561", {"start": v(123.33, -148) * mm, "end": v(124.44, -147.63) * mm});
            skLineSegment(sketch, "E562", {"start": v(124.44, -147.63) * mm, "end": v(125.56, -147.25) * mm});
            skLineSegment(sketch, "E563", {"start": v(125.56, -147.25) * mm, "end": v(126.67, -146.87) * mm});
            skLineSegment(sketch, "E564", {"start": v(126.67, -146.87) * mm, "end": v(127.78, -146.5) * mm});
            skLineSegment(sketch, "E565", {"start": v(127.78, -146.5) * mm, "end": v(128.89, -146.1) * mm});
            skLineSegment(sketch, "E566", {"start": v(128.89, -146.1) * mm, "end": v(130, -145.72) * mm});
            skLineSegment(sketch, "E567", {"start": v(130, -145.72) * mm, "end": v(131.11, -145.33) * mm});
            skLineSegment(sketch, "E568", {"start": v(131.11, -145.33) * mm, "end": v(132.22, -144.93) * mm});
            skLineSegment(sketch, "E569", {"start": v(132.22, -144.93) * mm, "end": v(133.33, -144.54) * mm});
            skLineSegment(sketch, "E570", {"start": v(133.33, -144.54) * mm, "end": v(134.44, -144.14) * mm});
            skLineSegment(sketch, "E571", {"start": v(134.44, -144.14) * mm, "end": v(135.56, -143.73) * mm});
            skLineSegment(sketch, "E572", {"start": v(135.56, -143.73) * mm, "end": v(136.67, -143.32) * mm});
            skLineSegment(sketch, "E573", {"start": v(136.67, -143.32) * mm, "end": v(137.78, -142.91) * mm});
            skLineSegment(sketch, "E574", {"start": v(137.78, -142.91) * mm, "end": v(138.89, -142.5) * mm});
            skLineSegment(sketch, "E575", {"start": v(138.89, -142.5) * mm, "end": v(140, -142.08) * mm});
            skLineSegment(sketch, "E576", {"start": v(140, -142.08) * mm, "end": v(141.11, -141.66) * mm});
            skLineSegment(sketch, "E577", {"start": v(141.11, -141.66) * mm, "end": v(142.22, -141.23) * mm});
            skLineSegment(sketch, "E578", {"start": v(142.22, -141.23) * mm, "end": v(143.33, -140.8) * mm});
            skLineSegment(sketch, "E579", {"start": v(143.33, -140.8) * mm, "end": v(144.44, -140.38) * mm});
            skLineSegment(sketch, "E580", {"start": v(144.44, -140.38) * mm, "end": v(145.56, -139.94) * mm});
            skLineSegment(sketch, "E581", {"start": v(145.56, -139.94) * mm, "end": v(146.67, -139.5) * mm});
            skLineSegment(sketch, "E582", {"start": v(146.67, -139.5) * mm, "end": v(147.78, -139.06) * mm});
            skLineSegment(sketch, "E583", {"start": v(147.78, -139.06) * mm, "end": v(148.89, -138.62) * mm});
            skLineSegment(sketch, "E584", {"start": v(148.89, -138.62) * mm, "end": v(150, -138.17) * mm});
            skLineSegment(sketch, "E585", {"start": v(150, -138.17) * mm, "end": v(151.11, -137.72) * mm});
            skLineSegment(sketch, "E586", {"start": v(151.11, -137.72) * mm, "end": v(152.22, -137.27) * mm});
            skLineSegment(sketch, "E587", {"start": v(152.22, -137.27) * mm, "end": v(153.33, -136.8) * mm});
            skLineSegment(sketch, "E588", {"start": v(153.33, -136.8) * mm, "end": v(154.44, -136.35) * mm});
            skLineSegment(sketch, "E589", {"start": v(154.44, -136.35) * mm, "end": v(155.56, -135.88) * mm});
            skLineSegment(sketch, "E590", {"start": v(155.56, -135.88) * mm, "end": v(156.67, -135.41) * mm});
            skLineSegment(sketch, "E591", {"start": v(156.67, -135.41) * mm, "end": v(157.78, -134.94) * mm});
            skLineSegment(sketch, "E592", {"start": v(157.78, -134.94) * mm, "end": v(158.89, -134.47) * mm});
            skLineSegment(sketch, "E593", {"start": v(158.89, -134.47) * mm, "end": v(160, -134) * mm});
            skLineSegment(sketch, "E594", {"start": v(160, -134) * mm, "end": v(161.11, -133.51) * mm});
            skLineSegment(sketch, "E595", {"start": v(161.11, -133.51) * mm, "end": v(162.22, -133.03) * mm});
            skLineSegment(sketch, "E596", {"start": v(162.22, -133.03) * mm, "end": v(163.33, -132.54) * mm});
            skLineSegment(sketch, "E597", {"start": v(163.33, -132.54) * mm, "end": v(164.44, -132.05) * mm});
            skLineSegment(sketch, "E598", {"start": v(164.44, -132.05) * mm, "end": v(165.56, -131.55) * mm});
            skLineSegment(sketch, "E599", {"start": v(165.56, -131.55) * mm, "end": v(166.67, -131.06) * mm});
            skLineSegment(sketch, "E600", {"start": v(166.67, -131.06) * mm, "end": v(167.78, -130.56) * mm});
            skLineSegment(sketch, "E601", {"start": v(167.78, -130.56) * mm, "end": v(168.89, -130.05) * mm});
            skLineSegment(sketch, "E602", {"start": v(168.89, -130.05) * mm, "end": v(170, -129.54) * mm});
            skLineSegment(sketch, "E603", {"start": v(170, -129.54) * mm, "end": v(171.11, -129.03) * mm});
            skLineSegment(sketch, "E604", {"start": v(171.11, -129.03) * mm, "end": v(172.22, -128.52) * mm});
            skLineSegment(sketch, "E605", {"start": v(172.22, -128.52) * mm, "end": v(173.33, -128) * mm});
            skLineSegment(sketch, "E606", {"start": v(173.33, -128) * mm, "end": v(174.44, -127.48) * mm});
            skLineSegment(sketch, "E607", {"start": v(174.44, -127.48) * mm, "end": v(175.56, -126.96) * mm});
            skLineSegment(sketch, "E608", {"start": v(175.56, -126.96) * mm, "end": v(176.67, -126.43) * mm});
            skLineSegment(sketch, "E609", {"start": v(176.67, -126.43) * mm, "end": v(177.78, -125.9) * mm});
            skLineSegment(sketch, "E610", {"start": v(177.78, -125.9) * mm, "end": v(178.89, -125.36) * mm});
            skLineSegment(sketch, "E611", {"start": v(178.89, -125.36) * mm, "end": v(180, -124.83) * mm});
            skLineSegment(sketch, "E612", {"start": v(180, -124.83) * mm, "end": v(181.11, -124.28) * mm});
            skLineSegment(sketch, "E613", {"start": v(181.11, -124.28) * mm, "end": v(182.22, -123.74) * mm});
            skLineSegment(sketch, "E614", {"start": v(182.22, -123.74) * mm, "end": v(183.33, -123.2) * mm});
            skLineSegment(sketch, "E615", {"start": v(183.33, -123.2) * mm, "end": v(184.44, -122.64) * mm});
            skLineSegment(sketch, "E616", {"start": v(184.44, -122.64) * mm, "end": v(185.56, -122.09) * mm});
            skLineSegment(sketch, "E617", {"start": v(185.56, -122.09) * mm, "end": v(186.67, -121.53) * mm});
            skLineSegment(sketch, "E618", {"start": v(186.67, -121.53) * mm, "end": v(187.78, -120.97) * mm});
            skLineSegment(sketch, "E619", {"start": v(187.78, -120.97) * mm, "end": v(188.89, -120.4) * mm});
            skLineSegment(sketch, "E620", {"start": v(188.89, -120.4) * mm, "end": v(190, -119.84) * mm});
            skLineSegment(sketch, "E621", {"start": v(190, -119.84) * mm, "end": v(191.11, -119.27) * mm});
            skLineSegment(sketch, "E622", {"start": v(191.11, -119.27) * mm, "end": v(192.22, -118.7) * mm});
            skLineSegment(sketch, "E623", {"start": v(192.22, -118.7) * mm, "end": v(193.33, -118.12) * mm});
            skLineSegment(sketch, "E624", {"start": v(193.33, -118.12) * mm, "end": v(194.44, -117.53) * mm});
            skLineSegment(sketch, "E625", {"start": v(194.44, -117.53) * mm, "end": v(195.56, -116.95) * mm});
            skLineSegment(sketch, "E626", {"start": v(195.56, -116.95) * mm, "end": v(196.67, -116.36) * mm});
            skLineSegment(sketch, "E627", {"start": v(196.67, -116.36) * mm, "end": v(197.78, -115.77) * mm});
            skLineSegment(sketch, "E628", {"start": v(197.78, -115.77) * mm, "end": v(198.89, -115.18) * mm});
            skLineSegment(sketch, "E629", {"start": v(198.89, -115.18) * mm, "end": v(200, -114.58) * mm});
            skLineSegment(sketch, "E630", {"start": v(200, -114.58) * mm, "end": v(201.11, -113.98) * mm});
            skLineSegment(sketch, "E631", {"start": v(201.11, -113.98) * mm, "end": v(202.22, -113.38) * mm});
            skLineSegment(sketch, "E632", {"start": v(202.22, -113.38) * mm, "end": v(203.33, -112.77) * mm});
            skLineSegment(sketch, "E633", {"start": v(203.33, -112.77) * mm, "end": v(204.44, -112.16) * mm});
            skLineSegment(sketch, "E634", {"start": v(204.44, -112.16) * mm, "end": v(205.56, -111.54) * mm});
            skLineSegment(sketch, "E635", {"start": v(205.56, -111.54) * mm, "end": v(206.67, -110.93) * mm});
            skLineSegment(sketch, "E636", {"start": v(206.67, -110.93) * mm, "end": v(207.78, -110.3) * mm});
            skLineSegment(sketch, "E637", {"start": v(207.78, -110.3) * mm, "end": v(208.89, -109.68) * mm});
            skLineSegment(sketch, "E638", {"start": v(208.89, -109.68) * mm, "end": v(210, -109.05) * mm});
            skLineSegment(sketch, "E639", {"start": v(210, -109.05) * mm, "end": v(211.11, -108.42) * mm});
            skLineSegment(sketch, "E640", {"start": v(211.11, -108.42) * mm, "end": v(212.22, -107.79) * mm});
            skLineSegment(sketch, "E641", {"start": v(212.22, -107.79) * mm, "end": v(213.33, -107.15) * mm});
            skLineSegment(sketch, "E642", {"start": v(213.33, -107.15) * mm, "end": v(214.44, -106.51) * mm});
            skLineSegment(sketch, "E643", {"start": v(214.44, -106.51) * mm, "end": v(215.56, -105.87) * mm});
            skLineSegment(sketch, "E644", {"start": v(215.56, -105.87) * mm, "end": v(216.67, -105.22) * mm});
            skLineSegment(sketch, "E645", {"start": v(216.67, -105.22) * mm, "end": v(217.78, -104.57) * mm});
            skLineSegment(sketch, "E646", {"start": v(217.78, -104.57) * mm, "end": v(218.89, -103.91) * mm});
            skLineSegment(sketch, "E647", {"start": v(218.89, -103.91) * mm, "end": v(220, -103.26) * mm});
            skLineSegment(sketch, "E648", {"start": v(220, -103.26) * mm, "end": v(221.11, -102.6) * mm});
            skLineSegment(sketch, "E649", {"start": v(221.11, -102.6) * mm, "end": v(222.22, -101.93) * mm});
            skLineSegment(sketch, "E650", {"start": v(222.22, -101.93) * mm, "end": v(223.33, -101.27) * mm});
            skLineSegment(sketch, "E651", {"start": v(223.33, -101.27) * mm, "end": v(224.44, -100.6) * mm});
            skLineSegment(sketch, "E652", {"start": v(224.44, -100.6) * mm, "end": v(225.56, -99.92) * mm});
            skLineSegment(sketch, "E653", {"start": v(225.56, -99.92) * mm, "end": v(226.67, -99.24) * mm});
            skLineSegment(sketch, "E654", {"start": v(226.67, -99.24) * mm, "end": v(227.78, -98.56) * mm});
            skLineSegment(sketch, "E655", {"start": v(227.78, -98.56) * mm, "end": v(228.89, -97.88) * mm});
            skLineSegment(sketch, "E656", {"start": v(228.89, -97.88) * mm, "end": v(230, -97.2) * mm});
            skLineSegment(sketch, "E657", {"start": v(230, -97.2) * mm, "end": v(231.11, -96.5) * mm});
            skLineSegment(sketch, "E658", {"start": v(231.11, -96.5) * mm, "end": v(232.22, -95.8) * mm});
            skLineSegment(sketch, "E659", {"start": v(232.22, -95.8) * mm, "end": v(233.33, -95.1) * mm});
            skLineSegment(sketch, "E660", {"start": v(233.33, -95.1) * mm, "end": v(234.44, -94.4) * mm});
            skLineSegment(sketch, "E661", {"start": v(234.44, -94.4) * mm, "end": v(235.56, -93.7) * mm});
            skLineSegment(sketch, "E662", {"start": v(235.56, -93.7) * mm, "end": v(236.67, -93) * mm});
            skLineSegment(sketch, "E663", {"start": v(236.67, -93) * mm, "end": v(237.78, -92.29) * mm});
            skLineSegment(sketch, "E664", {"start": v(237.78, -92.29) * mm, "end": v(238.89, -91.57) * mm});
            skLineSegment(sketch, "E665", {"start": v(238.89, -91.57) * mm, "end": v(240, -90.86) * mm});
            skLineSegment(sketch, "E666", {"start": v(240, -90.86) * mm, "end": v(241.11, -90.13) * mm});
            skLineSegment(sketch, "E667", {"start": v(241.11, -90.13) * mm, "end": v(242.22, -89.41) * mm});
            skLineSegment(sketch, "E668", {"start": v(242.22, -89.41) * mm, "end": v(243.33, -88.68) * mm});
            skLineSegment(sketch, "E669", {"start": v(243.33, -88.68) * mm, "end": v(244.44, -87.95) * mm});
            skLineSegment(sketch, "E670", {"start": v(244.44, -87.95) * mm, "end": v(245.56, -87.22) * mm});
            skLineSegment(sketch, "E671", {"start": v(245.56, -87.22) * mm, "end": v(246.67, -86.48) * mm});
            skLineSegment(sketch, "E672", {"start": v(246.67, -86.48) * mm, "end": v(247.78, -85.74) * mm});
            skLineSegment(sketch, "E673", {"start": v(247.78, -85.74) * mm, "end": v(248.89, -85) * mm});
            skLineSegment(sketch, "E674", {"start": v(248.89, -85) * mm, "end": v(250, -84.25) * mm});
            skLineSegment(sketch, "E675", {"start": v(250, -84.25) * mm, "end": v(251.11, -83.5) * mm});
            skLineSegment(sketch, "E676", {"start": v(251.11, -83.5) * mm, "end": v(252.22, -82.75) * mm});
            skLineSegment(sketch, "E677", {"start": v(252.22, -82.75) * mm, "end": v(253.33, -81.99) * mm});
            skLineSegment(sketch, "E678", {"start": v(253.33, -81.99) * mm, "end": v(254.44, -81.23) * mm});
            skLineSegment(sketch, "E679", {"start": v(254.44, -81.23) * mm, "end": v(255.56, -80.46) * mm});
            skLineSegment(sketch, "E680", {"start": v(255.56, -80.46) * mm, "end": v(256.67, -79.7) * mm});
            skLineSegment(sketch, "E681", {"start": v(256.67, -79.7) * mm, "end": v(257.78, -78.93) * mm});
            skLineSegment(sketch, "E682", {"start": v(257.78, -78.93) * mm, "end": v(258.89, -78.15) * mm});
            skLineSegment(sketch, "E683", {"start": v(258.89, -78.15) * mm, "end": v(260, -77.38) * mm});
            skLineSegment(sketch, "E684", {"start": v(260, -77.38) * mm, "end": v(261.11, -76.6) * mm});
            skLineSegment(sketch, "E685", {"start": v(261.11, -76.6) * mm, "end": v(262.22, -75.81) * mm});
            skLineSegment(sketch, "E686", {"start": v(262.22, -75.81) * mm, "end": v(263.33, -75.02) * mm});
            skLineSegment(sketch, "E687", {"start": v(263.33, -75.02) * mm, "end": v(264.44, -74.23) * mm});
            skLineSegment(sketch, "E688", {"start": v(264.44, -74.23) * mm, "end": v(265.56, -73.44) * mm});
            skLineSegment(sketch, "E689", {"start": v(265.56, -73.44) * mm, "end": v(266.67, -72.64) * mm});
            skLineSegment(sketch, "E690", {"start": v(266.67, -72.64) * mm, "end": v(267.78, -71.84) * mm});
            skLineSegment(sketch, "E691", {"start": v(267.78, -71.84) * mm, "end": v(268.89, -71.04) * mm});
            skLineSegment(sketch, "E692", {"start": v(268.89, -71.04) * mm, "end": v(270, -70.23) * mm});
            skLineSegment(sketch, "E693", {"start": v(270, -70.23) * mm, "end": v(271.11, -69.42) * mm});
            skLineSegment(sketch, "E694", {"start": v(271.11, -69.42) * mm, "end": v(272.22, -68.6) * mm});
            skLineSegment(sketch, "E695", {"start": v(272.22, -68.6) * mm, "end": v(273.33, -67.79) * mm});
            skLineSegment(sketch, "E696", {"start": v(273.33, -67.79) * mm, "end": v(274.44, -66.97) * mm});
            skLineSegment(sketch, "E697", {"start": v(274.44, -66.97) * mm, "end": v(275.56, -66.15) * mm});
            skLineSegment(sketch, "E698", {"start": v(275.56, -66.15) * mm, "end": v(276.67, -65.32) * mm});
            skLineSegment(sketch, "E699", {"start": v(276.67, -65.32) * mm, "end": v(277.78, -64.49) * mm});
            skLineSegment(sketch, "E700", {"start": v(277.78, -64.49) * mm, "end": v(278.89, -63.65) * mm});
            skLineSegment(sketch, "E701", {"start": v(278.89, -63.65) * mm, "end": v(280, -62.82) * mm});
            skLineSegment(sketch, "E702", {"start": v(280, -62.82) * mm, "end": v(281.11, -61.98) * mm});
            skLineSegment(sketch, "E703", {"start": v(281.11, -61.98) * mm, "end": v(282.22, -61.13) * mm});
            skLineSegment(sketch, "E704", {"start": v(282.22, -61.13) * mm, "end": v(283.33, -60.29) * mm});
            skLineSegment(sketch, "E705", {"start": v(283.33, -60.29) * mm, "end": v(284.44, -59.44) * mm});
            skLineSegment(sketch, "E706", {"start": v(284.44, -59.44) * mm, "end": v(285.56, -58.58) * mm});
            skLineSegment(sketch, "E707", {"start": v(285.56, -58.58) * mm, "end": v(286.67, -57.72) * mm});
            skLineSegment(sketch, "E708", {"start": v(286.67, -57.72) * mm, "end": v(287.78, -56.86) * mm});
            skLineSegment(sketch, "E709", {"start": v(287.78, -56.86) * mm, "end": v(288.89, -56) * mm});
            skLineSegment(sketch, "E710", {"start": v(288.89, -56) * mm, "end": v(290, -55.13) * mm});
            skLineSegment(sketch, "E711", {"start": v(290, -55.13) * mm, "end": v(291.11, -54.26) * mm});
            skLineSegment(sketch, "E712", {"start": v(291.11, -54.26) * mm, "end": v(292.22, -53.39) * mm});
            skLineSegment(sketch, "E713", {"start": v(292.22, -53.39) * mm, "end": v(293.33, -52.51) * mm});
            skLineSegment(sketch, "E714", {"start": v(293.33, -52.51) * mm, "end": v(294.44, -51.63) * mm});
            skLineSegment(sketch, "E715", {"start": v(294.44, -51.63) * mm, "end": v(295.56, -50.75) * mm});
            skLineSegment(sketch, "E716", {"start": v(295.56, -50.75) * mm, "end": v(296.67, -49.86) * mm});
            skLineSegment(sketch, "E717", {"start": v(296.67, -49.86) * mm, "end": v(297.78, -48.97) * mm});
            skLineSegment(sketch, "E718", {"start": v(297.78, -48.97) * mm, "end": v(298.89, -48.08) * mm});
            skLineSegment(sketch, "E719", {"start": v(298.89, -48.08) * mm, "end": v(300, -47.18) * mm});
            skLineSegment(sketch, "E720", {"start": v(300, -47.18) * mm, "end": v(301.11, -46.28) * mm});
            skLineSegment(sketch, "E721", {"start": v(301.11, -46.28) * mm, "end": v(302.22, -45.38) * mm});
            skLineSegment(sketch, "E722", {"start": v(302.22, -45.38) * mm, "end": v(303.33, -44.47) * mm});
            skLineSegment(sketch, "E723", {"start": v(303.33, -44.47) * mm, "end": v(304.44, -43.56) * mm});
            skLineSegment(sketch, "E724", {"start": v(304.44, -43.56) * mm, "end": v(305.56, -42.65) * mm});
            skLineSegment(sketch, "E725", {"start": v(305.56, -42.65) * mm, "end": v(306.67, -41.73) * mm});
            skLineSegment(sketch, "E726", {"start": v(306.67, -41.73) * mm, "end": v(307.78, -40.8) * mm});
            skLineSegment(sketch, "E727", {"start": v(307.78, -40.8) * mm, "end": v(308.89, -39.88) * mm});
            skLineSegment(sketch, "E728", {"start": v(308.89, -39.88) * mm, "end": v(310, -38.96) * mm});
            skLineSegment(sketch, "E729", {"start": v(310, -38.96) * mm, "end": v(311.11, -38.03) * mm});
            skLineSegment(sketch, "E730", {"start": v(311.11, -38.03) * mm, "end": v(312.22, -37.1) * mm});
            skLineSegment(sketch, "E731", {"start": v(312.22, -37.1) * mm, "end": v(313.33, -36.16) * mm});
            skLineSegment(sketch, "E732", {"start": v(313.33, -36.16) * mm, "end": v(314.44, -35.22) * mm});
            skLineSegment(sketch, "E733", {"start": v(314.44, -35.22) * mm, "end": v(315.56, -34.27) * mm});
            skLineSegment(sketch, "E734", {"start": v(315.56, -34.27) * mm, "end": v(316.67, -33.33) * mm});
            skLineSegment(sketch, "E735", {"start": v(316.67, -33.33) * mm, "end": v(317.78, -32.38) * mm});
            skLineSegment(sketch, "E736", {"start": v(317.78, -32.38) * mm, "end": v(318.89, -31.42) * mm});
            skLineSegment(sketch, "E737", {"start": v(318.89, -31.42) * mm, "end": v(320, -30.46) * mm});
            skLineSegment(sketch, "E738", {"start": v(320, -30.46) * mm, "end": v(321.11, -29.5) * mm});
            skLineSegment(sketch, "E739", {"start": v(321.11, -29.5) * mm, "end": v(322.22, -28.54) * mm});
            skLineSegment(sketch, "E740", {"start": v(322.22, -28.54) * mm, "end": v(323.33, -27.57) * mm});
            skLineSegment(sketch, "E741", {"start": v(323.33, -27.57) * mm, "end": v(324.44, -26.6) * mm});
            skLineSegment(sketch, "E742", {"start": v(324.44, -26.6) * mm, "end": v(325.56, -25.63) * mm});
            skLineSegment(sketch, "E743", {"start": v(325.56, -25.63) * mm, "end": v(326.67, -24.65) * mm});
            skLineSegment(sketch, "E744", {"start": v(326.67, -24.65) * mm, "end": v(327.78, -23.67) * mm});
            skLineSegment(sketch, "E745", {"start": v(327.78, -23.67) * mm, "end": v(328.89, -22.69) * mm});
            skLineSegment(sketch, "E746", {"start": v(328.89, -22.69) * mm, "end": v(330, -21.7) * mm});
            skLineSegment(sketch, "E747", {"start": v(330, -21.7) * mm, "end": v(331.11, -20.71) * mm});
            skLineSegment(sketch, "E748", {"start": v(331.11, -20.71) * mm, "end": v(332.22, -19.72) * mm});
            skLineSegment(sketch, "E749", {"start": v(332.22, -19.72) * mm, "end": v(333.33, -18.72) * mm});
            skLineSegment(sketch, "E750", {"start": v(333.33, -18.72) * mm, "end": v(334.44, -17.72) * mm});
            skLineSegment(sketch, "E751", {"start": v(334.44, -17.72) * mm, "end": v(335.56, -16.72) * mm});
            skLineSegment(sketch, "E752", {"start": v(335.56, -16.72) * mm, "end": v(336.67, -15.71) * mm});
            skLineSegment(sketch, "E753", {"start": v(336.67, -15.71) * mm, "end": v(337.78, -14.7) * mm});
            skLineSegment(sketch, "E754", {"start": v(337.78, -14.7) * mm, "end": v(338.89, -13.69) * mm});
            skLineSegment(sketch, "E755", {"start": v(338.89, -13.69) * mm, "end": v(340, -12.67) * mm});
            skLineSegment(sketch, "E756", {"start": v(340, -12.67) * mm, "end": v(341.11, -11.65) * mm});
            skLineSegment(sketch, "E757", {"start": v(341.11, -11.65) * mm, "end": v(342.22, -10.63) * mm});
            skLineSegment(sketch, "E758", {"start": v(342.22, -10.63) * mm, "end": v(343.33, -9.6) * mm});
            skLineSegment(sketch, "E759", {"start": v(343.33, -9.6) * mm, "end": v(344.44, -8.57) * mm});
            skLineSegment(sketch, "E760", {"start": v(344.44, -8.57) * mm, "end": v(345.56, -7.54) * mm});
            skLineSegment(sketch, "E761", {"start": v(345.56, -7.54) * mm, "end": v(346.67, -6.5) * mm});
            skLineSegment(sketch, "E762", {"start": v(346.67, -6.5) * mm, "end": v(347.78, -5.46) * mm});
            skLineSegment(sketch, "E763", {"start": v(347.78, -5.46) * mm, "end": v(348.89, -4.42) * mm});
            skLineSegment(sketch, "E764", {"start": v(348.89, -4.42) * mm, "end": v(350, -3.37) * mm});
            skLineSegment(sketch, "E765", {"start": v(350, -3.37) * mm, "end": v(351.11, -2.32) * mm});
            skLineSegment(sketch, "E766", {"start": v(351.11, -2.32) * mm, "end": v(352.22, -1.27) * mm});
            skLineSegment(sketch, "E767", {"start": v(352.22, -1.27) * mm, "end": v(353.33, -0.2) * mm});
            skLineSegment(sketch, "E768", {"start": v(353.33, -0.2) * mm, "end": v(354.44, 0.85) * mm});
            skLineSegment(sketch, "E769", {"start": v(354.44, 0.85) * mm, "end": v(355.56, 1.91) * mm});
            skLineSegment(sketch, "E770", {"start": v(355.56, 1.91) * mm, "end": v(356.67, 2.98) * mm});
            skLineSegment(sketch, "E771", {"start": v(356.67, 2.98) * mm, "end": v(357.78, 4.05) * mm});
            skLineSegment(sketch, "E772", {"start": v(357.78, 4.05) * mm, "end": v(358.89, 5.12) * mm});
            skLineSegment(sketch, "E773", {"start": v(358.89, 5.12) * mm, "end": v(360, 6.2) * mm});
            skLineSegment(sketch, "E774", {"start": v(360, 6.2) * mm, "end": v(361.11, 7.28) * mm});
            skLineSegment(sketch, "E775", {"start": v(361.11, 7.28) * mm, "end": v(362.22, 8.36) * mm});
            skLineSegment(sketch, "E776", {"start": v(362.22, 8.36) * mm, "end": v(363.33, 9.45) * mm});
            skLineSegment(sketch, "E777", {"start": v(363.33, 9.45) * mm, "end": v(364.44, 10.54) * mm});
            skLineSegment(sketch, "E778", {"start": v(364.44, 10.54) * mm, "end": v(365.56, 11.63) * mm});
            skLineSegment(sketch, "E779", {"start": v(365.56, 11.63) * mm, "end": v(366.67, 12.73) * mm});
            skLineSegment(sketch, "E780", {"start": v(366.67, 12.73) * mm, "end": v(367.78, 13.83) * mm});
            skLineSegment(sketch, "E781", {"start": v(367.78, 13.83) * mm, "end": v(368.89, 14.93) * mm});
            skLineSegment(sketch, "E782", {"start": v(368.89, 14.93) * mm, "end": v(370, 16.04) * mm});
            skLineSegment(sketch, "E783", {"start": v(370, 16.04) * mm, "end": v(371.11, 17.15) * mm});
            skLineSegment(sketch, "E784", {"start": v(371.11, 17.15) * mm, "end": v(372.22, 18.26) * mm});
            skLineSegment(sketch, "E785", {"start": v(372.22, 18.26) * mm, "end": v(373.33, 19.38) * mm});
            skLineSegment(sketch, "E786", {"start": v(373.33, 19.38) * mm, "end": v(374.44, 20.5) * mm});
            skLineSegment(sketch, "E787", {"start": v(374.44, 20.5) * mm, "end": v(375.56, 21.63) * mm});
            skLineSegment(sketch, "E788", {"start": v(375.56, 21.63) * mm, "end": v(376.67, 22.75) * mm});
            skLineSegment(sketch, "E789", {"start": v(376.67, 22.75) * mm, "end": v(377.78, 23.88) * mm});
            skLineSegment(sketch, "E790", {"start": v(377.78, 23.88) * mm, "end": v(378.89, 25.02) * mm});
            skLineSegment(sketch, "E791", {"start": v(378.89, 25.02) * mm, "end": v(380, 26.15) * mm});
            skLineSegment(sketch, "E792", {"start": v(380, 26.15) * mm, "end": v(381.11, 27.3) * mm});
            skLineSegment(sketch, "E793", {"start": v(381.11, 27.3) * mm, "end": v(382.22, 28.43) * mm});
            skLineSegment(sketch, "E794", {"start": v(382.22, 28.43) * mm, "end": v(383.33, 29.58) * mm});
            skLineSegment(sketch, "E795", {"start": v(383.33, 29.58) * mm, "end": v(384.44, 30.73) * mm});
            skLineSegment(sketch, "E796", {"start": v(384.44, 30.73) * mm, "end": v(385.56, 31.88) * mm});
            skLineSegment(sketch, "E797", {"start": v(385.56, 31.88) * mm, "end": v(386.67, 33.04) * mm});
            skLineSegment(sketch, "E798", {"start": v(386.67, 33.04) * mm, "end": v(387.78, 34.2) * mm});
            skLineSegment(sketch, "E799", {"start": v(387.78, 34.2) * mm, "end": v(388.89, 35.36) * mm});
            skLineSegment(sketch, "E800", {"start": v(388.89, 35.36) * mm, "end": v(390, 36.53) * mm});
            skLineSegment(sketch, "E801", {"start": v(390, 36.53) * mm, "end": v(391.11, 37.7) * mm});
            skLineSegment(sketch, "E802", {"start": v(391.11, 37.7) * mm, "end": v(392.22, 38.87) * mm});
            skLineSegment(sketch, "E803", {"start": v(392.22, 38.87) * mm, "end": v(393.33, 40.05) * mm});
            skLineSegment(sketch, "E804", {"start": v(393.33, 40.05) * mm, "end": v(394.44, 41.23) * mm});
            skLineSegment(sketch, "E805", {"start": v(394.44, 41.23) * mm, "end": v(395.56, 42.41) * mm});
            skLineSegment(sketch, "E806", {"start": v(395.56, 42.41) * mm, "end": v(396.67, 43.6) * mm});
            skLineSegment(sketch, "E807", {"start": v(396.67, 43.6) * mm, "end": v(397.78, 44.8) * mm});
            skLineSegment(sketch, "E808", {"start": v(397.78, 44.8) * mm, "end": v(398.89, 45.98) * mm});
            skLineSegment(sketch, "E809", {"start": v(398.89, 45.98) * mm, "end": v(400, 47.18) * mm});
            skLineSegment(sketch, "E810", {"start": v(400, 47.18) * mm, "end": v(401.11, 48.38) * mm});
            skLineSegment(sketch, "E811", {"start": v(401.11, 48.38) * mm, "end": v(402.22, 49.58) * mm});
            skLineSegment(sketch, "E812", {"start": v(402.22, 49.58) * mm, "end": v(403.33, 50.8) * mm});
            skLineSegment(sketch, "E813", {"start": v(403.33, 50.8) * mm, "end": v(404.44, 52) * mm});
            skLineSegment(sketch, "E814", {"start": v(404.44, 52) * mm, "end": v(405.56, 53.21) * mm});
            skLineSegment(sketch, "E815", {"start": v(405.56, 53.21) * mm, "end": v(406.67, 54.43) * mm});
            skLineSegment(sketch, "E816", {"start": v(406.67, 54.43) * mm, "end": v(407.78, 55.65) * mm});
            skLineSegment(sketch, "E817", {"start": v(407.78, 55.65) * mm, "end": v(408.89, 56.87) * mm});
            skLineSegment(sketch, "E818", {"start": v(408.89, 56.87) * mm, "end": v(410, 58.1) * mm});
            skLineSegment(sketch, "E819", {"start": v(410, 58.1) * mm, "end": v(411.11, 59.33) * mm});
            skLineSegment(sketch, "E820", {"start": v(411.11, 59.33) * mm, "end": v(412.22, 60.56) * mm});
            skLineSegment(sketch, "E821", {"start": v(412.22, 60.56) * mm, "end": v(413.33, 61.8) * mm});
            skLineSegment(sketch, "E822", {"start": v(413.33, 61.8) * mm, "end": v(414.44, 63.04) * mm});
            skLineSegment(sketch, "E823", {"start": v(414.44, 63.04) * mm, "end": v(415.56, 64.28) * mm});
            skLineSegment(sketch, "E824", {"start": v(415.56, 64.28) * mm, "end": v(416.67, 65.53) * mm});
            skLineSegment(sketch, "E825", {"start": v(416.67, 65.53) * mm, "end": v(417.78, 66.78) * mm});
            skLineSegment(sketch, "E826", {"start": v(417.78, 66.78) * mm, "end": v(418.89, 68.03) * mm});
            skLineSegment(sketch, "E827", {"start": v(418.89, 68.03) * mm, "end": v(420, 69.29) * mm});
            skLineSegment(sketch, "E828", {"start": v(420, 69.29) * mm, "end": v(421.11, 70.55) * mm});
            skLineSegment(sketch, "E829", {"start": v(421.11, 70.55) * mm, "end": v(422.22, 71.81) * mm});
            skLineSegment(sketch, "E830", {"start": v(422.22, 71.81) * mm, "end": v(423.33, 73.08) * mm});
            skLineSegment(sketch, "E831", {"start": v(423.33, 73.08) * mm, "end": v(424.44, 74.35) * mm});
            skLineSegment(sketch, "E832", {"start": v(424.44, 74.35) * mm, "end": v(425.56, 75.62) * mm});
            skLineSegment(sketch, "E833", {"start": v(425.56, 75.62) * mm, "end": v(426.67, 76.9) * mm});
            skLineSegment(sketch, "E834", {"start": v(426.67, 76.9) * mm, "end": v(427.78, 78.18) * mm});
            skLineSegment(sketch, "E835", {"start": v(427.78, 78.18) * mm, "end": v(428.89, 79.46) * mm});
            skLineSegment(sketch, "E836", {"start": v(428.89, 79.46) * mm, "end": v(430, 80.75) * mm});
            skLineSegment(sketch, "E837", {"start": v(430, 80.75) * mm, "end": v(431.11, 82.04) * mm});
            skLineSegment(sketch, "E838", {"start": v(431.11, 82.04) * mm, "end": v(432.22, 83.33) * mm});
            skLineSegment(sketch, "E839", {"start": v(432.22, 83.33) * mm, "end": v(433.33, 84.63) * mm});
            skLineSegment(sketch, "E840", {"start": v(433.33, 84.63) * mm, "end": v(434.44, 85.93) * mm});
            skLineSegment(sketch, "E841", {"start": v(434.44, 85.93) * mm, "end": v(435.56, 87.23) * mm});
            skLineSegment(sketch, "E842", {"start": v(435.56, 87.23) * mm, "end": v(436.67, 88.53) * mm});
            skLineSegment(sketch, "E843", {"start": v(436.67, 88.53) * mm, "end": v(437.78, 89.84) * mm});
            skLineSegment(sketch, "E844", {"start": v(437.78, 89.84) * mm, "end": v(438.89, 91.16) * mm});
            skLineSegment(sketch, "E845", {"start": v(438.89, 91.16) * mm, "end": v(440, 92.47) * mm});
            skLineSegment(sketch, "E846", {"start": v(440, 92.47) * mm, "end": v(441.11, 93.8) * mm});
            skLineSegment(sketch, "E847", {"start": v(441.11, 93.8) * mm, "end": v(442.22, 95.12) * mm});
            skLineSegment(sketch, "E848", {"start": v(442.22, 95.12) * mm, "end": v(443.33, 96.44) * mm});
            skLineSegment(sketch, "E849", {"start": v(443.33, 96.44) * mm, "end": v(444.44, 97.77) * mm});
            skLineSegment(sketch, "E850", {"start": v(444.44, 97.77) * mm, "end": v(445.56, 99.1) * mm});
            skLineSegment(sketch, "E851", {"start": v(445.56, 99.1) * mm, "end": v(446.67, 100.44) * mm});
            skLineSegment(sketch, "E852", {"start": v(446.67, 100.44) * mm, "end": v(447.78, 101.78) * mm});
            skLineSegment(sketch, "E853", {"start": v(447.78, 101.78) * mm, "end": v(448.89, 103.12) * mm});
            skLineSegment(sketch, "E854", {"start": v(448.89, 103.12) * mm, "end": v(450, 104.47) * mm});
            skLineSegment(sketch, "E855", {"start": v(450, 104.47) * mm, "end": v(451.11, 105.82) * mm});
            skLineSegment(sketch, "E856", {"start": v(451.11, 105.82) * mm, "end": v(452.22, 107.17) * mm});
            skLineSegment(sketch, "E857", {"start": v(452.22, 107.17) * mm, "end": v(453.33, 108.53) * mm});
            skLineSegment(sketch, "E858", {"start": v(453.33, 108.53) * mm, "end": v(454.44, 109.89) * mm});
            skLineSegment(sketch, "E859", {"start": v(454.44, 109.89) * mm, "end": v(455.56, 111.25) * mm});
            skLineSegment(sketch, "E860", {"start": v(455.56, 111.25) * mm, "end": v(456.67, 112.62) * mm});
            skLineSegment(sketch, "E861", {"start": v(456.67, 112.62) * mm, "end": v(457.78, 113.99) * mm});
            skLineSegment(sketch, "E862", {"start": v(457.78, 113.99) * mm, "end": v(458.89, 115.36) * mm});
            skLineSegment(sketch, "E863", {"start": v(458.89, 115.36) * mm, "end": v(460, 116.74) * mm});
            skLineSegment(sketch, "E864", {"start": v(460, 116.74) * mm, "end": v(461.11, 118.12) * mm});
            skLineSegment(sketch, "E865", {"start": v(461.11, 118.12) * mm, "end": v(462.22, 119.5) * mm});
            skLineSegment(sketch, "E866", {"start": v(462.22, 119.5) * mm, "end": v(463.33, 120.89) * mm});
            skLineSegment(sketch, "E867", {"start": v(463.33, 120.89) * mm, "end": v(464.44, 122.28) * mm});
            skLineSegment(sketch, "E868", {"start": v(464.44, 122.28) * mm, "end": v(465.56, 123.67) * mm});
            skLineSegment(sketch, "E869", {"start": v(465.56, 123.67) * mm, "end": v(466.67, 125.07) * mm});
            skLineSegment(sketch, "E870", {"start": v(466.67, 125.07) * mm, "end": v(467.78, 126.47) * mm});
            skLineSegment(sketch, "E871", {"start": v(467.78, 126.47) * mm, "end": v(468.89, 127.87) * mm});
            skLineSegment(sketch, "E872", {"start": v(468.89, 127.87) * mm, "end": v(470, 129.27) * mm});
            skLineSegment(sketch, "E873", {"start": v(470, 129.27) * mm, "end": v(471.11, 130.68) * mm});
            skLineSegment(sketch, "E874", {"start": v(471.11, 130.68) * mm, "end": v(472.22, 132.1) * mm});
            skLineSegment(sketch, "E875", {"start": v(472.22, 132.1) * mm, "end": v(473.33, 133.51) * mm});
            skLineSegment(sketch, "E876", {"start": v(473.33, 133.51) * mm, "end": v(474.44, 134.93) * mm});
            skLineSegment(sketch, "E877", {"start": v(474.44, 134.93) * mm, "end": v(475.56, 136.36) * mm});
            skLineSegment(sketch, "E878", {"start": v(475.56, 136.36) * mm, "end": v(476.67, 137.78) * mm});
            skLineSegment(sketch, "E879", {"start": v(476.67, 137.78) * mm, "end": v(477.78, 139.21) * mm});
            skLineSegment(sketch, "E880", {"start": v(477.78, 139.21) * mm, "end": v(478.89, 140.64) * mm});
            skLineSegment(sketch, "E881", {"start": v(478.89, 140.64) * mm, "end": v(480, 142.08) * mm});
            skLineSegment(sketch, "E882", {"start": v(480, 142.08) * mm, "end": v(481.11, 143.52) * mm});
            skLineSegment(sketch, "E883", {"start": v(481.11, 143.52) * mm, "end": v(482.22, 144.96) * mm});
            skLineSegment(sketch, "E884", {"start": v(482.22, 144.96) * mm, "end": v(483.33, 146.4) * mm});
            skLineSegment(sketch, "E885", {"start": v(483.33, 146.4) * mm, "end": v(484.44, 147.86) * mm});
            skLineSegment(sketch, "E886", {"start": v(484.44, 147.86) * mm, "end": v(485.56, 149.31) * mm});
            skLineSegment(sketch, "E887", {"start": v(485.56, 149.31) * mm, "end": v(486.67, 150.77) * mm});
            skLineSegment(sketch, "E888", {"start": v(486.67, 150.77) * mm, "end": v(487.78, 152.23) * mm});
            skLineSegment(sketch, "E889", {"start": v(487.78, 152.23) * mm, "end": v(488.89, 153.69) * mm});
            skLineSegment(sketch, "E890", {"start": v(488.89, 153.69) * mm, "end": v(490, 155.16) * mm});
            skLineSegment(sketch, "E891", {"start": v(490, 155.16) * mm, "end": v(491.11, 156.63) * mm});
            skLineSegment(sketch, "E892", {"start": v(491.11, 156.63) * mm, "end": v(492.22, 158.1) * mm});
            skLineSegment(sketch, "E893", {"start": v(492.22, 158.1) * mm, "end": v(493.33, 159.57) * mm});
            skLineSegment(sketch, "E894", {"start": v(493.33, 159.57) * mm, "end": v(494.44, 161.05) * mm});
            skLineSegment(sketch, "E895", {"start": v(494.44, 161.05) * mm, "end": v(495.56, 162.54) * mm});
            skLineSegment(sketch, "E896", {"start": v(495.56, 162.54) * mm, "end": v(496.67, 164.02) * mm});
            skLineSegment(sketch, "E897", {"start": v(496.67, 164.02) * mm, "end": v(497.78, 165.51) * mm});
            skLineSegment(sketch, "E898", {"start": v(497.78, 165.51) * mm, "end": v(498.89, 167) * mm});
            skLineSegment(sketch, "E899", {"start": v(498.89, 167) * mm, "end": v(500, 168.5) * mm});
            skLineSegment(sketch, "E900", {"start": v(-500, 168.5) * mm, "end": v(500, 168.5) * mm});
            skPoint(sketch, "E901.endSnap0", {"position": v(0, 168.5) * mm});
            skPoint(sketch, "E902", {"position": v(0, 16.96) * mm});
            skSolve(sketch);
        }
        {
            var Q0;
            {var subQ0=sQuery(id+"F0.wireOp",EDGE,"E0");Q0=makeQuery(id+"F0.imprint","IMPRINT",FACE,{"disambiguationData":[TD([[makeQuery(id+"F0.imprint","IMPRINT",EDGE,{"derivedFrom":subQ0}),1.0]])]});}
            extrude(context, id + "F1", {"entities" : qUnion([Q0]), "depth" : 2 * mm});
        }
        {
            var Q0;
            Q0=sQuery(id+"F0.wireOp",VERTEX,"E902");
            var Q1;
            Q1=makeQuery(id+"F1.opExtrude","SWEPT_BODY",BODY,{"disambiguationData":[OSD([sQuery(id+"F0.wireOp",EDGE,"E0"),sQuery(id+"F0.wireOp",EDGE,"E1"),sQuery(id+"F0.wireOp",EDGE,"E2"),sQuery(id+"F0.wireOp",EDGE,"E3"),sQuery(id+"F0.wireOp",EDGE,"E4"),sQuery(id+"F0.wireOp",EDGE,"E5"),sQuery(id+"F0.wireOp",EDGE,"E6"),sQuery(id+"F0.wireOp",EDGE,"E7"),sQuery(id+"F0.wireOp",EDGE,"E8"),sQuery(id+"F0.wireOp",EDGE,"E9"),sQuery(id+"F0.wireOp",EDGE,"E10"),sQuery(id+"F0.wireOp",EDGE,"E11"),sQuery(id+"F0.wireOp",EDGE,"E12"),sQuery(id+"F0.wireOp",EDGE,"E13"),sQuery(id+"F0.wireOp",EDGE,"E14"),sQuery(id+"F0.wireOp",EDGE,"E15"),sQuery(id+"F0.wireOp",EDGE,"E16"),sQuery(id+"F0.wireOp",EDGE,"E17"),sQuery(id+"F0.wireOp",EDGE,"E18"),sQuery(id+"F0.wireOp",EDGE,"E19"),sQuery(id+"F0.wireOp",EDGE,"E20"),sQuery(id+"F0.wireOp",EDGE,"E21"),sQuery(id+"F0.wireOp",EDGE,"E22"),sQuery(id+"F0.wireOp",EDGE,"E23"),sQuery(id+"F0.wireOp",EDGE,"E24"),sQuery(id+"F0.wireOp",EDGE,"E25"),sQuery(id+"F0.wireOp",EDGE,"E26"),sQuery(id+"F0.wireOp",EDGE,"E27"),sQuery(id+"F0.wireOp",EDGE,"E28"),sQuery(id+"F0.wireOp",EDGE,"E29"),sQuery(id+"F0.wireOp",EDGE,"E30"),sQuery(id+"F0.wireOp",EDGE,"E31"),sQuery(id+"F0.wireOp",EDGE,"E32"),sQuery(id+"F0.wireOp",EDGE,"E33"),sQuery(id+"F0.wireOp",EDGE,"E34"),sQuery(id+"F0.wireOp",EDGE,"E35"),sQuery(id+"F0.wireOp",EDGE,"E36"),sQuery(id+"F0.wireOp",EDGE,"E37"),sQuery(id+"F0.wireOp",EDGE,"E38"),sQuery(id+"F0.wireOp",EDGE,"E39"),sQuery(id+"F0.wireOp",EDGE,"E40"),sQuery(id+"F0.wireOp",EDGE,"E41"),sQuery(id+"F0.wireOp",EDGE,"E42"),sQuery(id+"F0.wireOp",EDGE,"E43"),sQuery(id+"F0.wireOp",EDGE,"E44"),sQuery(id+"F0.wireOp",EDGE,"E45"),sQuery(id+"F0.wireOp",EDGE,"E46"),sQuery(id+"F0.wireOp",EDGE,"E47"),sQuery(id+"F0.wireOp",EDGE,"E48"),sQuery(id+"F0.wireOp",EDGE,"E49"),sQuery(id+"F0.wireOp",EDGE,"E50"),sQuery(id+"F0.wireOp",EDGE,"E51"),sQuery(id+"F0.wireOp",EDGE,"E52"),sQuery(id+"F0.wireOp",EDGE,"E53"),sQuery(id+"F0.wireOp",EDGE,"E54"),sQuery(id+"F0.wireOp",EDGE,"E55"),sQuery(id+"F0.wireOp",EDGE,"E56"),sQuery(id+"F0.wireOp",EDGE,"E57"),sQuery(id+"F0.wireOp",EDGE,"E58"),sQuery(id+"F0.wireOp",EDGE,"E59"),sQuery(id+"F0.wireOp",EDGE,"E60"),sQuery(id+"F0.wireOp",EDGE,"E61"),sQuery(id+"F0.wireOp",EDGE,"E62"),sQuery(id+"F0.wireOp",EDGE,"E63"),sQuery(id+"F0.wireOp",EDGE,"E64"),sQuery(id+"F0.wireOp",EDGE,"E65"),sQuery(id+"F0.wireOp",EDGE,"E66"),sQuery(id+"F0.wireOp",EDGE,"E67"),sQuery(id+"F0.wireOp",EDGE,"E68"),sQuery(id+"F0.wireOp",EDGE,"E69"),sQuery(id+"F0.wireOp",EDGE,"E70"),sQuery(id+"F0.wireOp",EDGE,"E71"),sQuery(id+"F0.wireOp",EDGE,"E72"),sQuery(id+"F0.wireOp",EDGE,"E73"),sQuery(id+"F0.wireOp",EDGE,"E74"),sQuery(id+"F0.wireOp",EDGE,"E75"),sQuery(id+"F0.wireOp",EDGE,"E76"),sQuery(id+"F0.wireOp",EDGE,"E77"),sQuery(id+"F0.wireOp",EDGE,"E78"),sQuery(id+"F0.wireOp",EDGE,"E79"),sQuery(id+"F0.wireOp",EDGE,"E80"),sQuery(id+"F0.wireOp",EDGE,"E81"),sQuery(id+"F0.wireOp",EDGE,"E82"),sQuery(id+"F0.wireOp",EDGE,"E83"),sQuery(id+"F0.wireOp",EDGE,"E84"),sQuery(id+"F0.wireOp",EDGE,"E85"),sQuery(id+"F0.wireOp",EDGE,"E86"),sQuery(id+"F0.wireOp",EDGE,"E87"),sQuery(id+"F0.wireOp",EDGE,"E88"),sQuery(id+"F0.wireOp",EDGE,"E89"),sQuery(id+"F0.wireOp",EDGE,"E90"),sQuery(id+"F0.wireOp",EDGE,"E91"),sQuery(id+"F0.wireOp",EDGE,"E92"),sQuery(id+"F0.wireOp",EDGE,"E93"),sQuery(id+"F0.wireOp",EDGE,"E94"),sQuery(id+"F0.wireOp",EDGE,"E95"),sQuery(id+"F0.wireOp",EDGE,"E96"),sQuery(id+"F0.wireOp",EDGE,"E97"),sQuery(id+"F0.wireOp",EDGE,"E98"),sQuery(id+"F0.wireOp",EDGE,"E99"),sQuery(id+"F0.wireOp",EDGE,"E100"),sQuery(id+"F0.wireOp",EDGE,"E101"),sQuery(id+"F0.wireOp",EDGE,"E102"),sQuery(id+"F0.wireOp",EDGE,"E103"),sQuery(id+"F0.wireOp",EDGE,"E104"),sQuery(id+"F0.wireOp",EDGE,"E105"),sQuery(id+"F0.wireOp",EDGE,"E106"),sQuery(id+"F0.wireOp",EDGE,"E107"),sQuery(id+"F0.wireOp",EDGE,"E108"),sQuery(id+"F0.wireOp",EDGE,"E109"),sQuery(id+"F0.wireOp",EDGE,"E110"),sQuery(id+"F0.wireOp",EDGE,"E111"),sQuery(id+"F0.wireOp",EDGE,"E112"),sQuery(id+"F0.wireOp",EDGE,"E113"),sQuery(id+"F0.wireOp",EDGE,"E114"),sQuery(id+"F0.wireOp",EDGE,"E115"),sQuery(id+"F0.wireOp",EDGE,"E116"),sQuery(id+"F0.wireOp",EDGE,"E117"),sQuery(id+"F0.wireOp",EDGE,"E118"),sQuery(id+"F0.wireOp",EDGE,"E119"),sQuery(id+"F0.wireOp",EDGE,"E120"),sQuery(id+"F0.wireOp",EDGE,"E121"),sQuery(id+"F0.wireOp",EDGE,"E122"),sQuery(id+"F0.wireOp",EDGE,"E123"),sQuery(id+"F0.wireOp",EDGE,"E124"),sQuery(id+"F0.wireOp",EDGE,"E125"),sQuery(id+"F0.wireOp",EDGE,"E126"),sQuery(id+"F0.wireOp",EDGE,"E127"),sQuery(id+"F0.wireOp",EDGE,"E128"),sQuery(id+"F0.wireOp",EDGE,"E129"),sQuery(id+"F0.wireOp",EDGE,"E130"),sQuery(id+"F0.wireOp",EDGE,"E131"),sQuery(id+"F0.wireOp",EDGE,"E132"),sQuery(id+"F0.wireOp",EDGE,"E133"),sQuery(id+"F0.wireOp",EDGE,"E134"),sQuery(id+"F0.wireOp",EDGE,"E135"),sQuery(id+"F0.wireOp",EDGE,"E136"),sQuery(id+"F0.wireOp",EDGE,"E137"),sQuery(id+"F0.wireOp",EDGE,"E138"),sQuery(id+"F0.wireOp",EDGE,"E139"),sQuery(id+"F0.wireOp",EDGE,"E140"),sQuery(id+"F0.wireOp",EDGE,"E141"),sQuery(id+"F0.wireOp",EDGE,"E142"),sQuery(id+"F0.wireOp",EDGE,"E143"),sQuery(id+"F0.wireOp",EDGE,"E144"),sQuery(id+"F0.wireOp",EDGE,"E145"),sQuery(id+"F0.wireOp",EDGE,"E146"),sQuery(id+"F0.wireOp",EDGE,"E147"),sQuery(id+"F0.wireOp",EDGE,"E148"),sQuery(id+"F0.wireOp",EDGE,"E149"),sQuery(id+"F0.wireOp",EDGE,"E150"),sQuery(id+"F0.wireOp",EDGE,"E151"),sQuery(id+"F0.wireOp",EDGE,"E152"),sQuery(id+"F0.wireOp",EDGE,"E153"),sQuery(id+"F0.wireOp",EDGE,"E154"),sQuery(id+"F0.wireOp",EDGE,"E155"),sQuery(id+"F0.wireOp",EDGE,"E156"),sQuery(id+"F0.wireOp",EDGE,"E157"),sQuery(id+"F0.wireOp",EDGE,"E158"),sQuery(id+"F0.wireOp",EDGE,"E159"),sQuery(id+"F0.wireOp",EDGE,"E160"),sQuery(id+"F0.wireOp",EDGE,"E161"),sQuery(id+"F0.wireOp",EDGE,"E162"),sQuery(id+"F0.wireOp",EDGE,"E163"),sQuery(id+"F0.wireOp",EDGE,"E164"),sQuery(id+"F0.wireOp",EDGE,"E165"),sQuery(id+"F0.wireOp",EDGE,"E166"),sQuery(id+"F0.wireOp",EDGE,"E167"),sQuery(id+"F0.wireOp",EDGE,"E168"),sQuery(id+"F0.wireOp",EDGE,"E169"),sQuery(id+"F0.wireOp",EDGE,"E170"),sQuery(id+"F0.wireOp",EDGE,"E171"),sQuery(id+"F0.wireOp",EDGE,"E172"),sQuery(id+"F0.wireOp",EDGE,"E173"),sQuery(id+"F0.wireOp",EDGE,"E174"),sQuery(id+"F0.wireOp",EDGE,"E175"),sQuery(id+"F0.wireOp",EDGE,"E176"),sQuery(id+"F0.wireOp",EDGE,"E177"),sQuery(id+"F0.wireOp",EDGE,"E178"),sQuery(id+"F0.wireOp",EDGE,"E179"),sQuery(id+"F0.wireOp",EDGE,"E180"),sQuery(id+"F0.wireOp",EDGE,"E181"),sQuery(id+"F0.wireOp",EDGE,"E182"),sQuery(id+"F0.wireOp",EDGE,"E183"),sQuery(id+"F0.wireOp",EDGE,"E184"),sQuery(id+"F0.wireOp",EDGE,"E185"),sQuery(id+"F0.wireOp",EDGE,"E186"),sQuery(id+"F0.wireOp",EDGE,"E187"),sQuery(id+"F0.wireOp",EDGE,"E188"),sQuery(id+"F0.wireOp",EDGE,"E189"),sQuery(id+"F0.wireOp",EDGE,"E190"),sQuery(id+"F0.wireOp",EDGE,"E191"),sQuery(id+"F0.wireOp",EDGE,"E192"),sQuery(id+"F0.wireOp",EDGE,"E193"),sQuery(id+"F0.wireOp",EDGE,"E194"),sQuery(id+"F0.wireOp",EDGE,"E195"),sQuery(id+"F0.wireOp",EDGE,"E196"),sQuery(id+"F0.wireOp",EDGE,"E197"),sQuery(id+"F0.wireOp",EDGE,"E198"),sQuery(id+"F0.wireOp",EDGE,"E199"),sQuery(id+"F0.wireOp",EDGE,"E200"),sQuery(id+"F0.wireOp",EDGE,"E201"),sQuery(id+"F0.wireOp",EDGE,"E202"),sQuery(id+"F0.wireOp",EDGE,"E203"),sQuery(id+"F0.wireOp",EDGE,"E204"),sQuery(id+"F0.wireOp",EDGE,"E205"),sQuery(id+"F0.wireOp",EDGE,"E206"),sQuery(id+"F0.wireOp",EDGE,"E207"),sQuery(id+"F0.wireOp",EDGE,"E208"),sQuery(id+"F0.wireOp",EDGE,"E209"),sQuery(id+"F0.wireOp",EDGE,"E210"),sQuery(id+"F0.wireOp",EDGE,"E211"),sQuery(id+"F0.wireOp",EDGE,"E212"),sQuery(id+"F0.wireOp",EDGE,"E213"),sQuery(id+"F0.wireOp",EDGE,"E214"),sQuery(id+"F0.wireOp",EDGE,"E215"),sQuery(id+"F0.wireOp",EDGE,"E216"),sQuery(id+"F0.wireOp",EDGE,"E217"),sQuery(id+"F0.wireOp",EDGE,"E218"),sQuery(id+"F0.wireOp",EDGE,"E219"),sQuery(id+"F0.wireOp",EDGE,"E220"),sQuery(id+"F0.wireOp",EDGE,"E221"),sQuery(id+"F0.wireOp",EDGE,"E222"),sQuery(id+"F0.wireOp",EDGE,"E223"),sQuery(id+"F0.wireOp",EDGE,"E224"),sQuery(id+"F0.wireOp",EDGE,"E225"),sQuery(id+"F0.wireOp",EDGE,"E226"),sQuery(id+"F0.wireOp",EDGE,"E227"),sQuery(id+"F0.wireOp",EDGE,"E228"),sQuery(id+"F0.wireOp",EDGE,"E229"),sQuery(id+"F0.wireOp",EDGE,"E230"),sQuery(id+"F0.wireOp",EDGE,"E231"),sQuery(id+"F0.wireOp",EDGE,"E232"),sQuery(id+"F0.wireOp",EDGE,"E233"),sQuery(id+"F0.wireOp",EDGE,"E234"),sQuery(id+"F0.wireOp",EDGE,"E235"),sQuery(id+"F0.wireOp",EDGE,"E236"),sQuery(id+"F0.wireOp",EDGE,"E237"),sQuery(id+"F0.wireOp",EDGE,"E238"),sQuery(id+"F0.wireOp",EDGE,"E239"),sQuery(id+"F0.wireOp",EDGE,"E240"),sQuery(id+"F0.wireOp",EDGE,"E241"),sQuery(id+"F0.wireOp",EDGE,"E242"),sQuery(id+"F0.wireOp",EDGE,"E243"),sQuery(id+"F0.wireOp",EDGE,"E244"),sQuery(id+"F0.wireOp",EDGE,"E245"),sQuery(id+"F0.wireOp",EDGE,"E246"),sQuery(id+"F0.wireOp",EDGE,"E247"),sQuery(id+"F0.wireOp",EDGE,"E248"),sQuery(id+"F0.wireOp",EDGE,"E249"),sQuery(id+"F0.wireOp",EDGE,"E250"),sQuery(id+"F0.wireOp",EDGE,"E251"),sQuery(id+"F0.wireOp",EDGE,"E252"),sQuery(id+"F0.wireOp",EDGE,"E253"),sQuery(id+"F0.wireOp",EDGE,"E254"),sQuery(id+"F0.wireOp",EDGE,"E255"),sQuery(id+"F0.wireOp",EDGE,"E256"),sQuery(id+"F0.wireOp",EDGE,"E257"),sQuery(id+"F0.wireOp",EDGE,"E258"),sQuery(id+"F0.wireOp",EDGE,"E259"),sQuery(id+"F0.wireOp",EDGE,"E260"),sQuery(id+"F0.wireOp",EDGE,"E261"),sQuery(id+"F0.wireOp",EDGE,"E262"),sQuery(id+"F0.wireOp",EDGE,"E263"),sQuery(id+"F0.wireOp",EDGE,"E264"),sQuery(id+"F0.wireOp",EDGE,"E265"),sQuery(id+"F0.wireOp",EDGE,"E266"),sQuery(id+"F0.wireOp",EDGE,"E267"),sQuery(id+"F0.wireOp",EDGE,"E268"),sQuery(id+"F0.wireOp",EDGE,"E269"),sQuery(id+"F0.wireOp",EDGE,"E270"),sQuery(id+"F0.wireOp",EDGE,"E271"),sQuery(id+"F0.wireOp",EDGE,"E272"),sQuery(id+"F0.wireOp",EDGE,"E273"),sQuery(id+"F0.wireOp",EDGE,"E274"),sQuery(id+"F0.wireOp",EDGE,"E275"),sQuery(id+"F0.wireOp",EDGE,"E276"),sQuery(id+"F0.wireOp",EDGE,"E277"),sQuery(id+"F0.wireOp",EDGE,"E278"),sQuery(id+"F0.wireOp",EDGE,"E279"),sQuery(id+"F0.wireOp",EDGE,"E280"),sQuery(id+"F0.wireOp",EDGE,"E281"),sQuery(id+"F0.wireOp",EDGE,"E282"),sQuery(id+"F0.wireOp",EDGE,"E283"),sQuery(id+"F0.wireOp",EDGE,"E284"),sQuery(id+"F0.wireOp",EDGE,"E285"),sQuery(id+"F0.wireOp",EDGE,"E286"),sQuery(id+"F0.wireOp",EDGE,"E287"),sQuery(id+"F0.wireOp",EDGE,"E288"),sQuery(id+"F0.wireOp",EDGE,"E289"),sQuery(id+"F0.wireOp",EDGE,"E290"),sQuery(id+"F0.wireOp",EDGE,"E291"),sQuery(id+"F0.wireOp",EDGE,"E292"),sQuery(id+"F0.wireOp",EDGE,"E293"),sQuery(id+"F0.wireOp",EDGE,"E294"),sQuery(id+"F0.wireOp",EDGE,"E295"),sQuery(id+"F0.wireOp",EDGE,"E296"),sQuery(id+"F0.wireOp",EDGE,"E297"),sQuery(id+"F0.wireOp",EDGE,"E298"),sQuery(id+"F0.wireOp",EDGE,"E299"),sQuery(id+"F0.wireOp",EDGE,"E300"),sQuery(id+"F0.wireOp",EDGE,"E301"),sQuery(id+"F0.wireOp",EDGE,"E302"),sQuery(id+"F0.wireOp",EDGE,"E303"),sQuery(id+"F0.wireOp",EDGE,"E304"),sQuery(id+"F0.wireOp",EDGE,"E305"),sQuery(id+"F0.wireOp",EDGE,"E306"),sQuery(id+"F0.wireOp",EDGE,"E307"),sQuery(id+"F0.wireOp",EDGE,"E308"),sQuery(id+"F0.wireOp",EDGE,"E309"),sQuery(id+"F0.wireOp",EDGE,"E310"),sQuery(id+"F0.wireOp",EDGE,"E311"),sQuery(id+"F0.wireOp",EDGE,"E312"),sQuery(id+"F0.wireOp",EDGE,"E313"),sQuery(id+"F0.wireOp",EDGE,"E314"),sQuery(id+"F0.wireOp",EDGE,"E315"),sQuery(id+"F0.wireOp",EDGE,"E316"),sQuery(id+"F0.wireOp",EDGE,"E317"),sQuery(id+"F0.wireOp",EDGE,"E318"),sQuery(id+"F0.wireOp",EDGE,"E319"),sQuery(id+"F0.wireOp",EDGE,"E320"),sQuery(id+"F0.wireOp",EDGE,"E321"),sQuery(id+"F0.wireOp",EDGE,"E322"),sQuery(id+"F0.wireOp",EDGE,"E323"),sQuery(id+"F0.wireOp",EDGE,"E324"),sQuery(id+"F0.wireOp",EDGE,"E325"),sQuery(id+"F0.wireOp",EDGE,"E326"),sQuery(id+"F0.wireOp",EDGE,"E327"),sQuery(id+"F0.wireOp",EDGE,"E328"),sQuery(id+"F0.wireOp",EDGE,"E329"),sQuery(id+"F0.wireOp",EDGE,"E330"),sQuery(id+"F0.wireOp",EDGE,"E331"),sQuery(id+"F0.wireOp",EDGE,"E332"),sQuery(id+"F0.wireOp",EDGE,"E333"),sQuery(id+"F0.wireOp",EDGE,"E334"),sQuery(id+"F0.wireOp",EDGE,"E335"),sQuery(id+"F0.wireOp",EDGE,"E336"),sQuery(id+"F0.wireOp",EDGE,"E337"),sQuery(id+"F0.wireOp",EDGE,"E338"),sQuery(id+"F0.wireOp",EDGE,"E339"),sQuery(id+"F0.wireOp",EDGE,"E340"),sQuery(id+"F0.wireOp",EDGE,"E341"),sQuery(id+"F0.wireOp",EDGE,"E342"),sQuery(id+"F0.wireOp",EDGE,"E343"),sQuery(id+"F0.wireOp",EDGE,"E344"),sQuery(id+"F0.wireOp",EDGE,"E345"),sQuery(id+"F0.wireOp",EDGE,"E346"),sQuery(id+"F0.wireOp",EDGE,"E347"),sQuery(id+"F0.wireOp",EDGE,"E348"),sQuery(id+"F0.wireOp",EDGE,"E349"),sQuery(id+"F0.wireOp",EDGE,"E350"),sQuery(id+"F0.wireOp",EDGE,"E351"),sQuery(id+"F0.wireOp",EDGE,"E352"),sQuery(id+"F0.wireOp",EDGE,"E353"),sQuery(id+"F0.wireOp",EDGE,"E354"),sQuery(id+"F0.wireOp",EDGE,"E355"),sQuery(id+"F0.wireOp",EDGE,"E356"),sQuery(id+"F0.wireOp",EDGE,"E357"),sQuery(id+"F0.wireOp",EDGE,"E358"),sQuery(id+"F0.wireOp",EDGE,"E359"),sQuery(id+"F0.wireOp",EDGE,"E360"),sQuery(id+"F0.wireOp",EDGE,"E361"),sQuery(id+"F0.wireOp",EDGE,"E362"),sQuery(id+"F0.wireOp",EDGE,"E363"),sQuery(id+"F0.wireOp",EDGE,"E364"),sQuery(id+"F0.wireOp",EDGE,"E365"),sQuery(id+"F0.wireOp",EDGE,"E366"),sQuery(id+"F0.wireOp",EDGE,"E367"),sQuery(id+"F0.wireOp",EDGE,"E368"),sQuery(id+"F0.wireOp",EDGE,"E369"),sQuery(id+"F0.wireOp",EDGE,"E370"),sQuery(id+"F0.wireOp",EDGE,"E371"),sQuery(id+"F0.wireOp",EDGE,"E372"),sQuery(id+"F0.wireOp",EDGE,"E373"),sQuery(id+"F0.wireOp",EDGE,"E374"),sQuery(id+"F0.wireOp",EDGE,"E375"),sQuery(id+"F0.wireOp",EDGE,"E376"),sQuery(id+"F0.wireOp",EDGE,"E377"),sQuery(id+"F0.wireOp",EDGE,"E378"),sQuery(id+"F0.wireOp",EDGE,"E379"),sQuery(id+"F0.wireOp",EDGE,"E380"),sQuery(id+"F0.wireOp",EDGE,"E381"),sQuery(id+"F0.wireOp",EDGE,"E382"),sQuery(id+"F0.wireOp",EDGE,"E383"),sQuery(id+"F0.wireOp",EDGE,"E384"),sQuery(id+"F0.wireOp",EDGE,"E385"),sQuery(id+"F0.wireOp",EDGE,"E386"),sQuery(id+"F0.wireOp",EDGE,"E387"),sQuery(id+"F0.wireOp",EDGE,"E388"),sQuery(id+"F0.wireOp",EDGE,"E389"),sQuery(id+"F0.wireOp",EDGE,"E390"),sQuery(id+"F0.wireOp",EDGE,"E391"),sQuery(id+"F0.wireOp",EDGE,"E392"),sQuery(id+"F0.wireOp",EDGE,"E393"),sQuery(id+"F0.wireOp",EDGE,"E394"),sQuery(id+"F0.wireOp",EDGE,"E395"),sQuery(id+"F0.wireOp",EDGE,"E396"),sQuery(id+"F0.wireOp",EDGE,"E397"),sQuery(id+"F0.wireOp",EDGE,"E398"),sQuery(id+"F0.wireOp",EDGE,"E399"),sQuery(id+"F0.wireOp",EDGE,"E400"),sQuery(id+"F0.wireOp",EDGE,"E401"),sQuery(id+"F0.wireOp",EDGE,"E402"),sQuery(id+"F0.wireOp",EDGE,"E403"),sQuery(id+"F0.wireOp",EDGE,"E404"),sQuery(id+"F0.wireOp",EDGE,"E405"),sQuery(id+"F0.wireOp",EDGE,"E406"),sQuery(id+"F0.wireOp",EDGE,"E407"),sQuery(id+"F0.wireOp",EDGE,"E408"),sQuery(id+"F0.wireOp",EDGE,"E409"),sQuery(id+"F0.wireOp",EDGE,"E410"),sQuery(id+"F0.wireOp",EDGE,"E411"),sQuery(id+"F0.wireOp",EDGE,"E412"),sQuery(id+"F0.wireOp",EDGE,"E413"),sQuery(id+"F0.wireOp",EDGE,"E414"),sQuery(id+"F0.wireOp",EDGE,"E415"),sQuery(id+"F0.wireOp",EDGE,"E416"),sQuery(id+"F0.wireOp",EDGE,"E417"),sQuery(id+"F0.wireOp",EDGE,"E418"),sQuery(id+"F0.wireOp",EDGE,"E419"),sQuery(id+"F0.wireOp",EDGE,"E420"),sQuery(id+"F0.wireOp",EDGE,"E421"),sQuery(id+"F0.wireOp",EDGE,"E422"),sQuery(id+"F0.wireOp",EDGE,"E423"),sQuery(id+"F0.wireOp",EDGE,"E424"),sQuery(id+"F0.wireOp",EDGE,"E425"),sQuery(id+"F0.wireOp",EDGE,"E426"),sQuery(id+"F0.wireOp",EDGE,"E427"),sQuery(id+"F0.wireOp",EDGE,"E428"),sQuery(id+"F0.wireOp",EDGE,"E429"),sQuery(id+"F0.wireOp",EDGE,"E430"),sQuery(id+"F0.wireOp",EDGE,"E431"),sQuery(id+"F0.wireOp",EDGE,"E432"),sQuery(id+"F0.wireOp",EDGE,"E433"),sQuery(id+"F0.wireOp",EDGE,"E434"),sQuery(id+"F0.wireOp",EDGE,"E435"),sQuery(id+"F0.wireOp",EDGE,"E436"),sQuery(id+"F0.wireOp",EDGE,"E437"),sQuery(id+"F0.wireOp",EDGE,"E438"),sQuery(id+"F0.wireOp",EDGE,"E439"),sQuery(id+"F0.wireOp",EDGE,"E440"),sQuery(id+"F0.wireOp",EDGE,"E441"),sQuery(id+"F0.wireOp",EDGE,"E442"),sQuery(id+"F0.wireOp",EDGE,"E443"),sQuery(id+"F0.wireOp",EDGE,"E444"),sQuery(id+"F0.wireOp",EDGE,"E445"),sQuery(id+"F0.wireOp",EDGE,"E446"),sQuery(id+"F0.wireOp",EDGE,"E447"),sQuery(id+"F0.wireOp",EDGE,"E448"),sQuery(id+"F0.wireOp",EDGE,"E449"),sQuery(id+"F0.wireOp",EDGE,"E450"),sQuery(id+"F0.wireOp",EDGE,"E451"),sQuery(id+"F0.wireOp",EDGE,"E452"),sQuery(id+"F0.wireOp",EDGE,"E453"),sQuery(id+"F0.wireOp",EDGE,"E454"),sQuery(id+"F0.wireOp",EDGE,"E455"),sQuery(id+"F0.wireOp",EDGE,"E456"),sQuery(id+"F0.wireOp",EDGE,"E457"),sQuery(id+"F0.wireOp",EDGE,"E458"),sQuery(id+"F0.wireOp",EDGE,"E459"),sQuery(id+"F0.wireOp",EDGE,"E460"),sQuery(id+"F0.wireOp",EDGE,"E461"),sQuery(id+"F0.wireOp",EDGE,"E462"),sQuery(id+"F0.wireOp",EDGE,"E463"),sQuery(id+"F0.wireOp",EDGE,"E464"),sQuery(id+"F0.wireOp",EDGE,"E465"),sQuery(id+"F0.wireOp",EDGE,"E466"),sQuery(id+"F0.wireOp",EDGE,"E467"),sQuery(id+"F0.wireOp",EDGE,"E468"),sQuery(id+"F0.wireOp",EDGE,"E469"),sQuery(id+"F0.wireOp",EDGE,"E470"),sQuery(id+"F0.wireOp",EDGE,"E471"),sQuery(id+"F0.wireOp",EDGE,"E472"),sQuery(id+"F0.wireOp",EDGE,"E473"),sQuery(id+"F0.wireOp",EDGE,"E474"),sQuery(id+"F0.wireOp",EDGE,"E475"),sQuery(id+"F0.wireOp",EDGE,"E476"),sQuery(id+"F0.wireOp",EDGE,"E477"),sQuery(id+"F0.wireOp",EDGE,"E478"),sQuery(id+"F0.wireOp",EDGE,"E479"),sQuery(id+"F0.wireOp",EDGE,"E480"),sQuery(id+"F0.wireOp",EDGE,"E481"),sQuery(id+"F0.wireOp",EDGE,"E482"),sQuery(id+"F0.wireOp",EDGE,"E483"),sQuery(id+"F0.wireOp",EDGE,"E484"),sQuery(id+"F0.wireOp",EDGE,"E485"),sQuery(id+"F0.wireOp",EDGE,"E486"),sQuery(id+"F0.wireOp",EDGE,"E487"),sQuery(id+"F0.wireOp",EDGE,"E488"),sQuery(id+"F0.wireOp",EDGE,"E489"),sQuery(id+"F0.wireOp",EDGE,"E490"),sQuery(id+"F0.wireOp",EDGE,"E491"),sQuery(id+"F0.wireOp",EDGE,"E492"),sQuery(id+"F0.wireOp",EDGE,"E493"),sQuery(id+"F0.wireOp",EDGE,"E494"),sQuery(id+"F0.wireOp",EDGE,"E495"),sQuery(id+"F0.wireOp",EDGE,"E496"),sQuery(id+"F0.wireOp",EDGE,"E497"),sQuery(id+"F0.wireOp",EDGE,"E498"),sQuery(id+"F0.wireOp",EDGE,"E499"),sQuery(id+"F0.wireOp",EDGE,"E500"),sQuery(id+"F0.wireOp",EDGE,"E501"),sQuery(id+"F0.wireOp",EDGE,"E502"),sQuery(id+"F0.wireOp",EDGE,"E503"),sQuery(id+"F0.wireOp",EDGE,"E504"),sQuery(id+"F0.wireOp",EDGE,"E505"),sQuery(id+"F0.wireOp",EDGE,"E506"),sQuery(id+"F0.wireOp",EDGE,"E507"),sQuery(id+"F0.wireOp",EDGE,"E508"),sQuery(id+"F0.wireOp",EDGE,"E509"),sQuery(id+"F0.wireOp",EDGE,"E510"),sQuery(id+"F0.wireOp",EDGE,"E511"),sQuery(id+"F0.wireOp",EDGE,"E512"),sQuery(id+"F0.wireOp",EDGE,"E513"),sQuery(id+"F0.wireOp",EDGE,"E514"),sQuery(id+"F0.wireOp",EDGE,"E515"),sQuery(id+"F0.wireOp",EDGE,"E516"),sQuery(id+"F0.wireOp",EDGE,"E517"),sQuery(id+"F0.wireOp",EDGE,"E518"),sQuery(id+"F0.wireOp",EDGE,"E519"),sQuery(id+"F0.wireOp",EDGE,"E520"),sQuery(id+"F0.wireOp",EDGE,"E521"),sQuery(id+"F0.wireOp",EDGE,"E522"),sQuery(id+"F0.wireOp",EDGE,"E523"),sQuery(id+"F0.wireOp",EDGE,"E524"),sQuery(id+"F0.wireOp",EDGE,"E525"),sQuery(id+"F0.wireOp",EDGE,"E526"),sQuery(id+"F0.wireOp",EDGE,"E527"),sQuery(id+"F0.wireOp",EDGE,"E528"),sQuery(id+"F0.wireOp",EDGE,"E529"),sQuery(id+"F0.wireOp",EDGE,"E530"),sQuery(id+"F0.wireOp",EDGE,"E531"),sQuery(id+"F0.wireOp",EDGE,"E532"),sQuery(id+"F0.wireOp",EDGE,"E533"),sQuery(id+"F0.wireOp",EDGE,"E534"),sQuery(id+"F0.wireOp",EDGE,"E535"),sQuery(id+"F0.wireOp",EDGE,"E536"),sQuery(id+"F0.wireOp",EDGE,"E537"),sQuery(id+"F0.wireOp",EDGE,"E538"),sQuery(id+"F0.wireOp",EDGE,"E539"),sQuery(id+"F0.wireOp",EDGE,"E540"),sQuery(id+"F0.wireOp",EDGE,"E541"),sQuery(id+"F0.wireOp",EDGE,"E542"),sQuery(id+"F0.wireOp",EDGE,"E543"),sQuery(id+"F0.wireOp",EDGE,"E544"),sQuery(id+"F0.wireOp",EDGE,"E545"),sQuery(id+"F0.wireOp",EDGE,"E546"),sQuery(id+"F0.wireOp",EDGE,"E547"),sQuery(id+"F0.wireOp",EDGE,"E548"),sQuery(id+"F0.wireOp",EDGE,"E549"),sQuery(id+"F0.wireOp",EDGE,"E550"),sQuery(id+"F0.wireOp",EDGE,"E551"),sQuery(id+"F0.wireOp",EDGE,"E552"),sQuery(id+"F0.wireOp",EDGE,"E553"),sQuery(id+"F0.wireOp",EDGE,"E554"),sQuery(id+"F0.wireOp",EDGE,"E555"),sQuery(id+"F0.wireOp",EDGE,"E556"),sQuery(id+"F0.wireOp",EDGE,"E557"),sQuery(id+"F0.wireOp",EDGE,"E558"),sQuery(id+"F0.wireOp",EDGE,"E559"),sQuery(id+"F0.wireOp",EDGE,"E560"),sQuery(id+"F0.wireOp",EDGE,"E561"),sQuery(id+"F0.wireOp",EDGE,"E562"),sQuery(id+"F0.wireOp",EDGE,"E563"),sQuery(id+"F0.wireOp",EDGE,"E564"),sQuery(id+"F0.wireOp",EDGE,"E565"),sQuery(id+"F0.wireOp",EDGE,"E566"),sQuery(id+"F0.wireOp",EDGE,"E567"),sQuery(id+"F0.wireOp",EDGE,"E568"),sQuery(id+"F0.wireOp",EDGE,"E569"),sQuery(id+"F0.wireOp",EDGE,"E570"),sQuery(id+"F0.wireOp",EDGE,"E571"),sQuery(id+"F0.wireOp",EDGE,"E572"),sQuery(id+"F0.wireOp",EDGE,"E573"),sQuery(id+"F0.wireOp",EDGE,"E574"),sQuery(id+"F0.wireOp",EDGE,"E575"),sQuery(id+"F0.wireOp",EDGE,"E576"),sQuery(id+"F0.wireOp",EDGE,"E577"),sQuery(id+"F0.wireOp",EDGE,"E578"),sQuery(id+"F0.wireOp",EDGE,"E579"),sQuery(id+"F0.wireOp",EDGE,"E580"),sQuery(id+"F0.wireOp",EDGE,"E581"),sQuery(id+"F0.wireOp",EDGE,"E582"),sQuery(id+"F0.wireOp",EDGE,"E583"),sQuery(id+"F0.wireOp",EDGE,"E584"),sQuery(id+"F0.wireOp",EDGE,"E585"),sQuery(id+"F0.wireOp",EDGE,"E586"),sQuery(id+"F0.wireOp",EDGE,"E587"),sQuery(id+"F0.wireOp",EDGE,"E588"),sQuery(id+"F0.wireOp",EDGE,"E589"),sQuery(id+"F0.wireOp",EDGE,"E590"),sQuery(id+"F0.wireOp",EDGE,"E591"),sQuery(id+"F0.wireOp",EDGE,"E592"),sQuery(id+"F0.wireOp",EDGE,"E593"),sQuery(id+"F0.wireOp",EDGE,"E594"),sQuery(id+"F0.wireOp",EDGE,"E595"),sQuery(id+"F0.wireOp",EDGE,"E596"),sQuery(id+"F0.wireOp",EDGE,"E597"),sQuery(id+"F0.wireOp",EDGE,"E598"),sQuery(id+"F0.wireOp",EDGE,"E599"),sQuery(id+"F0.wireOp",EDGE,"E600"),sQuery(id+"F0.wireOp",EDGE,"E601"),sQuery(id+"F0.wireOp",EDGE,"E602"),sQuery(id+"F0.wireOp",EDGE,"E603"),sQuery(id+"F0.wireOp",EDGE,"E604"),sQuery(id+"F0.wireOp",EDGE,"E605"),sQuery(id+"F0.wireOp",EDGE,"E606"),sQuery(id+"F0.wireOp",EDGE,"E607"),sQuery(id+"F0.wireOp",EDGE,"E608"),sQuery(id+"F0.wireOp",EDGE,"E609"),sQuery(id+"F0.wireOp",EDGE,"E610"),sQuery(id+"F0.wireOp",EDGE,"E611"),sQuery(id+"F0.wireOp",EDGE,"E612"),sQuery(id+"F0.wireOp",EDGE,"E613"),sQuery(id+"F0.wireOp",EDGE,"E614"),sQuery(id+"F0.wireOp",EDGE,"E615"),sQuery(id+"F0.wireOp",EDGE,"E616"),sQuery(id+"F0.wireOp",EDGE,"E617"),sQuery(id+"F0.wireOp",EDGE,"E618"),sQuery(id+"F0.wireOp",EDGE,"E619"),sQuery(id+"F0.wireOp",EDGE,"E620"),sQuery(id+"F0.wireOp",EDGE,"E621"),sQuery(id+"F0.wireOp",EDGE,"E622"),sQuery(id+"F0.wireOp",EDGE,"E623"),sQuery(id+"F0.wireOp",EDGE,"E624"),sQuery(id+"F0.wireOp",EDGE,"E625"),sQuery(id+"F0.wireOp",EDGE,"E626"),sQuery(id+"F0.wireOp",EDGE,"E627"),sQuery(id+"F0.wireOp",EDGE,"E628"),sQuery(id+"F0.wireOp",EDGE,"E629"),sQuery(id+"F0.wireOp",EDGE,"E630"),sQuery(id+"F0.wireOp",EDGE,"E631"),sQuery(id+"F0.wireOp",EDGE,"E632"),sQuery(id+"F0.wireOp",EDGE,"E633"),sQuery(id+"F0.wireOp",EDGE,"E634"),sQuery(id+"F0.wireOp",EDGE,"E635"),sQuery(id+"F0.wireOp",EDGE,"E636"),sQuery(id+"F0.wireOp",EDGE,"E637"),sQuery(id+"F0.wireOp",EDGE,"E638"),sQuery(id+"F0.wireOp",EDGE,"E639"),sQuery(id+"F0.wireOp",EDGE,"E640"),sQuery(id+"F0.wireOp",EDGE,"E641"),sQuery(id+"F0.wireOp",EDGE,"E642"),sQuery(id+"F0.wireOp",EDGE,"E643"),sQuery(id+"F0.wireOp",EDGE,"E644"),sQuery(id+"F0.wireOp",EDGE,"E645"),sQuery(id+"F0.wireOp",EDGE,"E646"),sQuery(id+"F0.wireOp",EDGE,"E647"),sQuery(id+"F0.wireOp",EDGE,"E648"),sQuery(id+"F0.wireOp",EDGE,"E649"),sQuery(id+"F0.wireOp",EDGE,"E650"),sQuery(id+"F0.wireOp",EDGE,"E651"),sQuery(id+"F0.wireOp",EDGE,"E652"),sQuery(id+"F0.wireOp",EDGE,"E653"),sQuery(id+"F0.wireOp",EDGE,"E654"),sQuery(id+"F0.wireOp",EDGE,"E655"),sQuery(id+"F0.wireOp",EDGE,"E656"),sQuery(id+"F0.wireOp",EDGE,"E657"),sQuery(id+"F0.wireOp",EDGE,"E658"),sQuery(id+"F0.wireOp",EDGE,"E659"),sQuery(id+"F0.wireOp",EDGE,"E660"),sQuery(id+"F0.wireOp",EDGE,"E661"),sQuery(id+"F0.wireOp",EDGE,"E662"),sQuery(id+"F0.wireOp",EDGE,"E663"),sQuery(id+"F0.wireOp",EDGE,"E664"),sQuery(id+"F0.wireOp",EDGE,"E665"),sQuery(id+"F0.wireOp",EDGE,"E666"),sQuery(id+"F0.wireOp",EDGE,"E667"),sQuery(id+"F0.wireOp",EDGE,"E668"),sQuery(id+"F0.wireOp",EDGE,"E669"),sQuery(id+"F0.wireOp",EDGE,"E670"),sQuery(id+"F0.wireOp",EDGE,"E671"),sQuery(id+"F0.wireOp",EDGE,"E672"),sQuery(id+"F0.wireOp",EDGE,"E673"),sQuery(id+"F0.wireOp",EDGE,"E674"),sQuery(id+"F0.wireOp",EDGE,"E675"),sQuery(id+"F0.wireOp",EDGE,"E676"),sQuery(id+"F0.wireOp",EDGE,"E677"),sQuery(id+"F0.wireOp",EDGE,"E678"),sQuery(id+"F0.wireOp",EDGE,"E679"),sQuery(id+"F0.wireOp",EDGE,"E680"),sQuery(id+"F0.wireOp",EDGE,"E681"),sQuery(id+"F0.wireOp",EDGE,"E682"),sQuery(id+"F0.wireOp",EDGE,"E683"),sQuery(id+"F0.wireOp",EDGE,"E684"),sQuery(id+"F0.wireOp",EDGE,"E685"),sQuery(id+"F0.wireOp",EDGE,"E686"),sQuery(id+"F0.wireOp",EDGE,"E687"),sQuery(id+"F0.wireOp",EDGE,"E688"),sQuery(id+"F0.wireOp",EDGE,"E689"),sQuery(id+"F0.wireOp",EDGE,"E690"),sQuery(id+"F0.wireOp",EDGE,"E691"),sQuery(id+"F0.wireOp",EDGE,"E692"),sQuery(id+"F0.wireOp",EDGE,"E693"),sQuery(id+"F0.wireOp",EDGE,"E694"),sQuery(id+"F0.wireOp",EDGE,"E695"),sQuery(id+"F0.wireOp",EDGE,"E696"),sQuery(id+"F0.wireOp",EDGE,"E697"),sQuery(id+"F0.wireOp",EDGE,"E698"),sQuery(id+"F0.wireOp",EDGE,"E699"),sQuery(id+"F0.wireOp",EDGE,"E700"),sQuery(id+"F0.wireOp",EDGE,"E701"),sQuery(id+"F0.wireOp",EDGE,"E702"),sQuery(id+"F0.wireOp",EDGE,"E703"),sQuery(id+"F0.wireOp",EDGE,"E704"),sQuery(id+"F0.wireOp",EDGE,"E705"),sQuery(id+"F0.wireOp",EDGE,"E706"),sQuery(id+"F0.wireOp",EDGE,"E707"),sQuery(id+"F0.wireOp",EDGE,"E708"),sQuery(id+"F0.wireOp",EDGE,"E709"),sQuery(id+"F0.wireOp",EDGE,"E710"),sQuery(id+"F0.wireOp",EDGE,"E711"),sQuery(id+"F0.wireOp",EDGE,"E712"),sQuery(id+"F0.wireOp",EDGE,"E713"),sQuery(id+"F0.wireOp",EDGE,"E714"),sQuery(id+"F0.wireOp",EDGE,"E715"),sQuery(id+"F0.wireOp",EDGE,"E716"),sQuery(id+"F0.wireOp",EDGE,"E717"),sQuery(id+"F0.wireOp",EDGE,"E718"),sQuery(id+"F0.wireOp",EDGE,"E719"),sQuery(id+"F0.wireOp",EDGE,"E720"),sQuery(id+"F0.wireOp",EDGE,"E721"),sQuery(id+"F0.wireOp",EDGE,"E722"),sQuery(id+"F0.wireOp",EDGE,"E723"),sQuery(id+"F0.wireOp",EDGE,"E724"),sQuery(id+"F0.wireOp",EDGE,"E725"),sQuery(id+"F0.wireOp",EDGE,"E726"),sQuery(id+"F0.wireOp",EDGE,"E727"),sQuery(id+"F0.wireOp",EDGE,"E728"),sQuery(id+"F0.wireOp",EDGE,"E729"),sQuery(id+"F0.wireOp",EDGE,"E730"),sQuery(id+"F0.wireOp",EDGE,"E731"),sQuery(id+"F0.wireOp",EDGE,"E732"),sQuery(id+"F0.wireOp",EDGE,"E733"),sQuery(id+"F0.wireOp",EDGE,"E734"),sQuery(id+"F0.wireOp",EDGE,"E735"),sQuery(id+"F0.wireOp",EDGE,"E736"),sQuery(id+"F0.wireOp",EDGE,"E737"),sQuery(id+"F0.wireOp",EDGE,"E738"),sQuery(id+"F0.wireOp",EDGE,"E739"),sQuery(id+"F0.wireOp",EDGE,"E740"),sQuery(id+"F0.wireOp",EDGE,"E741"),sQuery(id+"F0.wireOp",EDGE,"E742"),sQuery(id+"F0.wireOp",EDGE,"E743"),sQuery(id+"F0.wireOp",EDGE,"E744"),sQuery(id+"F0.wireOp",EDGE,"E745"),sQuery(id+"F0.wireOp",EDGE,"E746"),sQuery(id+"F0.wireOp",EDGE,"E747"),sQuery(id+"F0.wireOp",EDGE,"E748"),sQuery(id+"F0.wireOp",EDGE,"E749"),sQuery(id+"F0.wireOp",EDGE,"E750"),sQuery(id+"F0.wireOp",EDGE,"E751"),sQuery(id+"F0.wireOp",EDGE,"E752"),sQuery(id+"F0.wireOp",EDGE,"E753"),sQuery(id+"F0.wireOp",EDGE,"E754"),sQuery(id+"F0.wireOp",EDGE,"E755"),sQuery(id+"F0.wireOp",EDGE,"E756"),sQuery(id+"F0.wireOp",EDGE,"E757"),sQuery(id+"F0.wireOp",EDGE,"E758"),sQuery(id+"F0.wireOp",EDGE,"E759"),sQuery(id+"F0.wireOp",EDGE,"E760"),sQuery(id+"F0.wireOp",EDGE,"E761"),sQuery(id+"F0.wireOp",EDGE,"E762"),sQuery(id+"F0.wireOp",EDGE,"E763"),sQuery(id+"F0.wireOp",EDGE,"E764"),sQuery(id+"F0.wireOp",EDGE,"E765"),sQuery(id+"F0.wireOp",EDGE,"E766"),sQuery(id+"F0.wireOp",EDGE,"E767"),sQuery(id+"F0.wireOp",EDGE,"E768"),sQuery(id+"F0.wireOp",EDGE,"E769"),sQuery(id+"F0.wireOp",EDGE,"E770"),sQuery(id+"F0.wireOp",EDGE,"E771"),sQuery(id+"F0.wireOp",EDGE,"E772"),sQuery(id+"F0.wireOp",EDGE,"E773"),sQuery(id+"F0.wireOp",EDGE,"E774"),sQuery(id+"F0.wireOp",EDGE,"E775"),sQuery(id+"F0.wireOp",EDGE,"E776"),sQuery(id+"F0.wireOp",EDGE,"E777"),sQuery(id+"F0.wireOp",EDGE,"E778"),sQuery(id+"F0.wireOp",EDGE,"E779"),sQuery(id+"F0.wireOp",EDGE,"E780"),sQuery(id+"F0.wireOp",EDGE,"E781"),sQuery(id+"F0.wireOp",EDGE,"E782"),sQuery(id+"F0.wireOp",EDGE,"E783"),sQuery(id+"F0.wireOp",EDGE,"E784"),sQuery(id+"F0.wireOp",EDGE,"E785"),sQuery(id+"F0.wireOp",EDGE,"E786"),sQuery(id+"F0.wireOp",EDGE,"E787"),sQuery(id+"F0.wireOp",EDGE,"E788"),sQuery(id+"F0.wireOp",EDGE,"E789"),sQuery(id+"F0.wireOp",EDGE,"E790"),sQuery(id+"F0.wireOp",EDGE,"E791"),sQuery(id+"F0.wireOp",EDGE,"E792"),sQuery(id+"F0.wireOp",EDGE,"E793"),sQuery(id+"F0.wireOp",EDGE,"E794"),sQuery(id+"F0.wireOp",EDGE,"E795"),sQuery(id+"F0.wireOp",EDGE,"E796"),sQuery(id+"F0.wireOp",EDGE,"E797"),sQuery(id+"F0.wireOp",EDGE,"E798"),sQuery(id+"F0.wireOp",EDGE,"E799"),sQuery(id+"F0.wireOp",EDGE,"E800"),sQuery(id+"F0.wireOp",EDGE,"E801"),sQuery(id+"F0.wireOp",EDGE,"E802"),sQuery(id+"F0.wireOp",EDGE,"E803"),sQuery(id+"F0.wireOp",EDGE,"E804"),sQuery(id+"F0.wireOp",EDGE,"E805"),sQuery(id+"F0.wireOp",EDGE,"E806"),sQuery(id+"F0.wireOp",EDGE,"E807"),sQuery(id+"F0.wireOp",EDGE,"E808"),sQuery(id+"F0.wireOp",EDGE,"E809"),sQuery(id+"F0.wireOp",EDGE,"E810"),sQuery(id+"F0.wireOp",EDGE,"E811"),sQuery(id+"F0.wireOp",EDGE,"E812"),sQuery(id+"F0.wireOp",EDGE,"E813"),sQuery(id+"F0.wireOp",EDGE,"E814"),sQuery(id+"F0.wireOp",EDGE,"E815"),sQuery(id+"F0.wireOp",EDGE,"E816"),sQuery(id+"F0.wireOp",EDGE,"E817"),sQuery(id+"F0.wireOp",EDGE,"E818"),sQuery(id+"F0.wireOp",EDGE,"E819"),sQuery(id+"F0.wireOp",EDGE,"E820"),sQuery(id+"F0.wireOp",EDGE,"E821"),sQuery(id+"F0.wireOp",EDGE,"E822"),sQuery(id+"F0.wireOp",EDGE,"E823"),sQuery(id+"F0.wireOp",EDGE,"E824"),sQuery(id+"F0.wireOp",EDGE,"E825"),sQuery(id+"F0.wireOp",EDGE,"E826"),sQuery(id+"F0.wireOp",EDGE,"E827"),sQuery(id+"F0.wireOp",EDGE,"E828"),sQuery(id+"F0.wireOp",EDGE,"E829"),sQuery(id+"F0.wireOp",EDGE,"E830"),sQuery(id+"F0.wireOp",EDGE,"E831"),sQuery(id+"F0.wireOp",EDGE,"E832"),sQuery(id+"F0.wireOp",EDGE,"E833"),sQuery(id+"F0.wireOp",EDGE,"E834"),sQuery(id+"F0.wireOp",EDGE,"E835"),sQuery(id+"F0.wireOp",EDGE,"E836"),sQuery(id+"F0.wireOp",EDGE,"E837"),sQuery(id+"F0.wireOp",EDGE,"E838"),sQuery(id+"F0.wireOp",EDGE,"E839"),sQuery(id+"F0.wireOp",EDGE,"E840"),sQuery(id+"F0.wireOp",EDGE,"E841"),sQuery(id+"F0.wireOp",EDGE,"E842"),sQuery(id+"F0.wireOp",EDGE,"E843"),sQuery(id+"F0.wireOp",EDGE,"E844"),sQuery(id+"F0.wireOp",EDGE,"E845"),sQuery(id+"F0.wireOp",EDGE,"E846"),sQuery(id+"F0.wireOp",EDGE,"E847"),sQuery(id+"F0.wireOp",EDGE,"E848"),sQuery(id+"F0.wireOp",EDGE,"E849"),sQuery(id+"F0.wireOp",EDGE,"E850"),sQuery(id+"F0.wireOp",EDGE,"E851"),sQuery(id+"F0.wireOp",EDGE,"E852"),sQuery(id+"F0.wireOp",EDGE,"E853"),sQuery(id+"F0.wireOp",EDGE,"E854"),sQuery(id+"F0.wireOp",EDGE,"E855"),sQuery(id+"F0.wireOp",EDGE,"E856"),sQuery(id+"F0.wireOp",EDGE,"E857"),sQuery(id+"F0.wireOp",EDGE,"E858"),sQuery(id+"F0.wireOp",EDGE,"E859"),sQuery(id+"F0.wireOp",EDGE,"E860"),sQuery(id+"F0.wireOp",EDGE,"E861"),sQuery(id+"F0.wireOp",EDGE,"E862"),sQuery(id+"F0.wireOp",EDGE,"E863"),sQuery(id+"F0.wireOp",EDGE,"E864"),sQuery(id+"F0.wireOp",EDGE,"E865"),sQuery(id+"F0.wireOp",EDGE,"E866"),sQuery(id+"F0.wireOp",EDGE,"E867"),sQuery(id+"F0.wireOp",EDGE,"E868"),sQuery(id+"F0.wireOp",EDGE,"E869"),sQuery(id+"F0.wireOp",EDGE,"E870"),sQuery(id+"F0.wireOp",EDGE,"E871"),sQuery(id+"F0.wireOp",EDGE,"E872"),sQuery(id+"F0.wireOp",EDGE,"E873"),sQuery(id+"F0.wireOp",EDGE,"E874"),sQuery(id+"F0.wireOp",EDGE,"E875"),sQuery(id+"F0.wireOp",EDGE,"E876"),sQuery(id+"F0.wireOp",EDGE,"E877"),sQuery(id+"F0.wireOp",EDGE,"E878"),sQuery(id+"F0.wireOp",EDGE,"E879"),sQuery(id+"F0.wireOp",EDGE,"E880"),sQuery(id+"F0.wireOp",EDGE,"E881"),sQuery(id+"F0.wireOp",EDGE,"E882"),sQuery(id+"F0.wireOp",EDGE,"E883"),sQuery(id+"F0.wireOp",EDGE,"E884"),sQuery(id+"F0.wireOp",EDGE,"E885"),sQuery(id+"F0.wireOp",EDGE,"E886"),sQuery(id+"F0.wireOp",EDGE,"E887"),sQuery(id+"F0.wireOp",EDGE,"E888"),sQuery(id+"F0.wireOp",EDGE,"E889"),sQuery(id+"F0.wireOp",EDGE,"E890"),sQuery(id+"F0.wireOp",EDGE,"E891"),sQuery(id+"F0.wireOp",EDGE,"E892"),sQuery(id+"F0.wireOp",EDGE,"E893"),sQuery(id+"F0.wireOp",EDGE,"E894"),sQuery(id+"F0.wireOp",EDGE,"E895"),sQuery(id+"F0.wireOp",EDGE,"E896"),sQuery(id+"F0.wireOp",EDGE,"E897"),sQuery(id+"F0.wireOp",EDGE,"E898"),sQuery(id+"F0.wireOp",EDGE,"E899"),sQuery(id+"F0.wireOp",EDGE,"E900")])]});
            hole(context, id + "F2", {"style" : HoleStyle.SIMPLE, "endStyle" : HoleEndStyle.THROUGH, "oppositeDirection" : true, "holeDiameter" : 25 * mm, "tappedDepth" : 12 * mm, "tapClearance" : 3, "locations" : qUnion([Q0]), "scope" : qUnion([Q1])});
        }
    });
